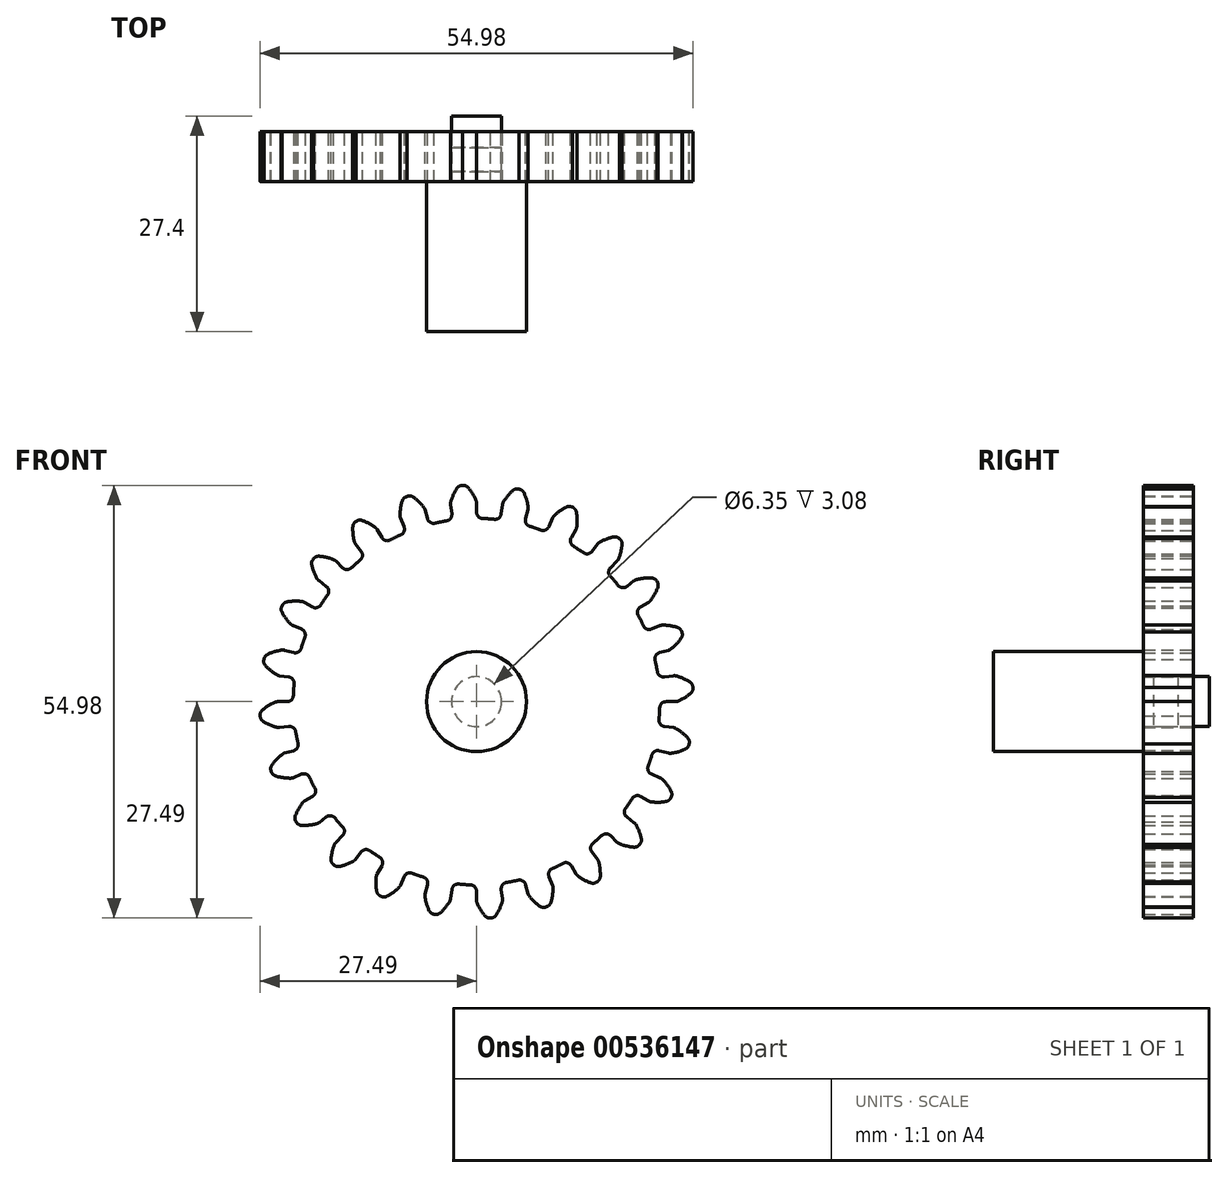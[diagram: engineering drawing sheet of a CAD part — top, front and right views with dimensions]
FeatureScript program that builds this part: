
annotation { "Feature Type Name" : "Feature", "Feature Type Description" : "" }
export const myFeature = defineFeature(function(context is Context, id is Id, definition is map)
    precondition{}
    {
        {
            var Q0;
            Q0=qCreatedBy(makeId("Front.planeOp"),FACE);
            var sketch = newSketch(context, id + "F0", { "sketchPlane" : qUnion([Q0])});
            skArc(sketch, "E0", {"start": v(-3.8, 22.97) * mm, "mid": v(-4.54, 22.84) * mm, "end": v(-5.28, 22.68) * mm});
            skArc(sketch, "E1.trimOffspring", {"start": v(-0.06, 25.55) * mm, "mid": v(-0.5, 26.41) * mm, "end": v(-1.06, 27.2) * mm});
            skLineSegment(sketch, "E2", {"start": v(0, 25.25) * mm, "end": v(0, 24.06) * mm});
            skLineSegment(sketch, "E3", {"start": v(-1.67, 27.49) * mm, "end": v(-1.8, 27.49) * mm});
            skLineSegment(sketch, "E4.MirrorCS", {"start": v(-1.93, 27.47) * mm, "end": v(-1.8, 27.49) * mm});
            skArc(sketch, "E5.MirrorCS", {"start": v(-3.28, 25.34) * mm, "mid": v(-2.95, 26.25) * mm, "end": v(-2.5, 27.1) * mm});
            skLineSegment(sketch, "E6.MirrorCS", {"start": v(-3.3, 25.03) * mm, "end": v(-3.14, 23.86) * mm});
            skPoint(sketch, "E7.visualSharp", {"position": v(-3.04, 23.08) * mm});
            skArc(sketch, "E8.filletArc", {"start": v(-3.8, 22.97) * mm, "mid": v(-3.3, 23.28) * mm, "end": v(-3.14, 23.86) * mm});
            skPoint(sketch, "E9.visualSharp", {"position": v(-3.32, 25.18) * mm});
            skArc(sketch, "E9.filletArc", {"start": v(-3.28, 25.34) * mm, "mid": v(-3.3, 25.19) * mm, "end": v(-3.3, 25.03) * mm});
            skPoint(sketch, "E10.visualSharp", {"position": v(-2.28, 27.42) * mm});
            skArc(sketch, "E10.filletArc", {"start": v(-1.93, 27.47) * mm, "mid": v(-2.25, 27.35) * mm, "end": v(-2.5, 27.1) * mm});
            skPoint(sketch, "E11.visualSharp", {"position": v(0, 25.4) * mm});
            skArc(sketch, "E11.filletArc", {"start": v(0, 25.25) * mm, "mid": v(-0.02, 25.4) * mm, "end": v(-0.06, 25.55) * mm});
            skPoint(sketch, "E12.visualSharp", {"position": v(0, 23.28) * mm});
            skArc(sketch, "E12.filletArc", {"start": v(0, 24.06) * mm, "mid": v(0.22, 23.51) * mm, "end": v(0.77, 23.27) * mm});
            skPoint(sketch, "E13.visualSharp", {"position": v(-1.31, 27.49) * mm});
            skArc(sketch, "E13.filletArc", {"start": v(-1.06, 27.2) * mm, "mid": v(-1.33, 27.41) * mm, "end": v(-1.67, 27.49) * mm});
            skArc(sketch, "E14.1.0", {"start": v(-9.61, 21.2) * mm, "mid": v(-9.2, 21.64) * mm, "end": v(-9.2, 22.23) * mm});
            skLineSegment(sketch, "E14.1.1", {"start": v(-9.66, 23.33) * mm, "end": v(-9.2, 22.23) * mm});
            skArc(sketch, "E14.1.2", {"start": v(-9.72, 23.63) * mm, "mid": v(-9.7, 23.47) * mm, "end": v(-9.66, 23.33) * mm});
            skArc(sketch, "E14.1.3", {"start": v(-9.72, 23.63) * mm, "mid": v(-9.65, 24.6) * mm, "end": v(-9.43, 25.54) * mm});
            skArc(sketch, "E14.1.4", {"start": v(-8.98, 26.03) * mm, "mid": v(-9.26, 25.83) * mm, "end": v(-9.43, 25.54) * mm});
            skLineSegment(sketch, "E14.1.5", {"start": v(-8.98, 26.03) * mm, "end": v(-8.85, 26.08) * mm});
            skLineSegment(sketch, "E14.1.6", {"start": v(-8.73, 26.12) * mm, "end": v(-8.85, 26.08) * mm});
            skArc(sketch, "E14.1.7", {"start": v(-8.07, 26) * mm, "mid": v(-8.38, 26.13) * mm, "end": v(-8.73, 26.12) * mm});
            skArc(sketch, "E14.1.8", {"start": v(-6.67, 24.67) * mm, "mid": v(-7.32, 25.39) * mm, "end": v(-8.07, 26) * mm});
            skArc(sketch, "E14.1.9", {"start": v(-6.53, 24.39) * mm, "mid": v(-6.59, 24.53) * mm, "end": v(-6.67, 24.67) * mm});
            skLineSegment(sketch, "E14.1.10", {"start": v(-6.53, 24.39) * mm, "end": v(-6.23, 23.24) * mm});
            skArc(sketch, "E14.1.11", {"start": v(-6.23, 23.24) * mm, "mid": v(-5.87, 22.77) * mm, "end": v(-5.28, 22.68) * mm});
            skArc(sketch, "E14.2.0", {"start": v(-14.78, 18) * mm, "mid": v(-14.5, 18.52) * mm, "end": v(-14.65, 19.1) * mm});
            skLineSegment(sketch, "E14.2.1", {"start": v(-15.37, 20.03) * mm, "end": v(-14.65, 19.1) * mm});
            skArc(sketch, "E14.2.2", {"start": v(-15.5, 20.3) * mm, "mid": v(-15.45, 20.16) * mm, "end": v(-15.37, 20.03) * mm});
            skArc(sketch, "E14.2.3", {"start": v(-15.5, 20.3) * mm, "mid": v(-15.69, 21.26) * mm, "end": v(-15.72, 22.23) * mm});
            skArc(sketch, "E14.2.4", {"start": v(-15.4, 22.82) * mm, "mid": v(-15.63, 22.56) * mm, "end": v(-15.72, 22.23) * mm});
            skLineSegment(sketch, "E14.2.5", {"start": v(-15.4, 22.82) * mm, "end": v(-15.3, 22.9) * mm});
            skLineSegment(sketch, "E14.2.6", {"start": v(-15.19, 22.97) * mm, "end": v(-15.3, 22.9) * mm});
            skArc(sketch, "E14.2.7", {"start": v(-14.52, 23.03) * mm, "mid": v(-14.86, 23.07) * mm, "end": v(-15.19, 22.97) * mm});
            skArc(sketch, "E14.2.8", {"start": v(-12.83, 22.1) * mm, "mid": v(-13.64, 22.63) * mm, "end": v(-14.52, 23.03) * mm});
            skArc(sketch, "E14.2.9", {"start": v(-12.62, 21.87) * mm, "mid": v(-12.71, 22) * mm, "end": v(-12.83, 22.1) * mm});
            skLineSegment(sketch, "E14.2.10", {"start": v(-12.62, 21.87) * mm, "end": v(-12.03, 20.84) * mm});
            skArc(sketch, "E14.2.11", {"start": v(-12.03, 20.84) * mm, "mid": v(-11.56, 20.47) * mm, "end": v(-10.97, 20.54) * mm});
            skArc(sketch, "E15.2.3.0", {"start": v(-18.93, 13.56) * mm, "mid": v(-18.79, 14.14) * mm, "end": v(-19.1, 14.65) * mm});
            skLineSegment(sketch, "E15.4.3.0", {"start": v(-20.03, 15.37) * mm, "end": v(-19.1, 14.65) * mm});
            skArc(sketch, "E15.7.3.0", {"start": v(-20.23, 15.6) * mm, "mid": v(-20.14, 15.48) * mm, "end": v(-20.03, 15.37) * mm});
            skArc(sketch, "E15.11.3.0", {"start": v(-20.23, 15.6) * mm, "mid": v(-20.65, 16.48) * mm, "end": v(-20.93, 17.4) * mm});
            skArc(sketch, "E15.15.3.0", {"start": v(-20.79, 18.06) * mm, "mid": v(-20.93, 17.75) * mm, "end": v(-20.93, 17.4) * mm});
            skLineSegment(sketch, "E15.19.3.0", {"start": v(-20.79, 18.06) * mm, "end": v(-20.7, 18.16) * mm});
            skLineSegment(sketch, "E15.22.3.0", {"start": v(-20.62, 18.25) * mm, "end": v(-20.7, 18.16) * mm});
            skArc(sketch, "E15.25.3.0", {"start": v(-19.99, 18.48) * mm, "mid": v(-20.33, 18.44) * mm, "end": v(-20.62, 18.25) * mm});
            skArc(sketch, "E15.29.3.0", {"start": v(-18.11, 18.02) * mm, "mid": v(-19.03, 18.33) * mm, "end": v(-19.99, 18.48) * mm});
            skArc(sketch, "E15.33.3.0", {"start": v(-17.85, 17.85) * mm, "mid": v(-17.97, 17.95) * mm, "end": v(-18.11, 18.02) * mm});
            skLineSegment(sketch, "E15.37.3.0", {"start": v(-17.85, 17.85) * mm, "end": v(-17.02, 17.02) * mm});
            skArc(sketch, "E15.40.3.0", {"start": v(-17.02, 17.02) * mm, "mid": v(-16.47, 16.78) * mm, "end": v(-15.91, 17) * mm});
            skArc(sketch, "E15.2.4.0", {"start": v(-21.8, 8.2) * mm, "mid": v(-21.8, 8.8) * mm, "end": v(-22.23, 9.2) * mm});
            skLineSegment(sketch, "E15.4.4.0", {"start": v(-23.33, 9.66) * mm, "end": v(-22.23, 9.2) * mm});
            skArc(sketch, "E15.7.4.0", {"start": v(-23.58, 9.83) * mm, "mid": v(-23.46, 9.74) * mm, "end": v(-23.33, 9.66) * mm});
            skArc(sketch, "E15.11.4.0", {"start": v(-23.58, 9.83) * mm, "mid": v(-24.21, 10.57) * mm, "end": v(-24.72, 11.4) * mm});
            skArc(sketch, "E15.15.4.0", {"start": v(-24.75, 12.06) * mm, "mid": v(-24.81, 11.72) * mm, "end": v(-24.72, 11.4) * mm});
            skLineSegment(sketch, "E15.19.4.0", {"start": v(-24.75, 12.06) * mm, "end": v(-24.7, 12.18) * mm});
            skLineSegment(sketch, "E15.22.4.0", {"start": v(-24.64, 12.3) * mm, "end": v(-24.7, 12.18) * mm});
            skArc(sketch, "E15.25.4.0", {"start": v(-24.09, 12.68) * mm, "mid": v(-24.4, 12.55) * mm, "end": v(-24.64, 12.3) * mm});
            skArc(sketch, "E15.29.4.0", {"start": v(-22.16, 12.72) * mm, "mid": v(-23.12, 12.78) * mm, "end": v(-24.09, 12.68) * mm});
            skArc(sketch, "E15.33.4.0", {"start": v(-21.87, 12.62) * mm, "mid": v(-22, 12.69) * mm, "end": v(-22.16, 12.72) * mm});
            skLineSegment(sketch, "E15.37.4.0", {"start": v(-21.87, 12.62) * mm, "end": v(-20.84, 12.03) * mm});
            skArc(sketch, "E15.40.4.0", {"start": v(-20.84, 12.03) * mm, "mid": v(-20.25, 11.95) * mm, "end": v(-19.77, 12.3) * mm});
            skArc(sketch, "E15.2.5.0", {"start": v(-23.17, 2.28) * mm, "mid": v(-23.34, 2.85) * mm, "end": v(-23.86, 3.14) * mm});
            skLineSegment(sketch, "E15.4.5.0", {"start": v(-25.03, 3.3) * mm, "end": v(-23.86, 3.14) * mm});
            skArc(sketch, "E15.7.5.0", {"start": v(-25.32, 3.4) * mm, "mid": v(-25.18, 3.33) * mm, "end": v(-25.03, 3.3) * mm});
            skArc(sketch, "E15.11.5.0", {"start": v(-25.32, 3.4) * mm, "mid": v(-26.12, 3.94) * mm, "end": v(-26.83, 4.6) * mm});
            skArc(sketch, "E15.15.5.0", {"start": v(-27.03, 5.24) * mm, "mid": v(-27, 4.9) * mm, "end": v(-26.83, 4.6) * mm});
            skLineSegment(sketch, "E15.19.5.0", {"start": v(-27.03, 5.24) * mm, "end": v(-27.01, 5.37) * mm});
            skLineSegment(sketch, "E15.22.5.0", {"start": v(-26.98, 5.5) * mm, "end": v(-27.01, 5.37) * mm});
            skArc(sketch, "E15.25.5.0", {"start": v(-26.55, 6.01) * mm, "mid": v(-26.82, 5.8) * mm, "end": v(-26.98, 5.5) * mm});
            skArc(sketch, "E15.29.5.0", {"start": v(-24.7, 6.55) * mm, "mid": v(-25.64, 6.36) * mm, "end": v(-26.55, 6.01) * mm});
            skArc(sketch, "E15.33.5.0", {"start": v(-24.39, 6.53) * mm, "mid": v(-24.54, 6.56) * mm, "end": v(-24.7, 6.55) * mm});
            skLineSegment(sketch, "E15.37.5.0", {"start": v(-24.39, 6.53) * mm, "end": v(-23.24, 6.23) * mm});
            skArc(sketch, "E15.40.5.0", {"start": v(-23.24, 6.23) * mm, "mid": v(-22.65, 6.3) * mm, "end": v(-22.28, 6.76) * mm});
            skArc(sketch, "E15.2.6.0", {"start": v(-22.97, -3.8) * mm, "mid": v(-23.28, -3.3) * mm, "end": v(-23.86, -3.14) * mm});
            skLineSegment(sketch, "E15.4.6.0", {"start": v(-25.03, -3.3) * mm, "end": v(-23.86, -3.14) * mm});
            skArc(sketch, "E15.7.6.0", {"start": v(-25.34, -3.28) * mm, "mid": v(-25.19, -3.3) * mm, "end": v(-25.03, -3.3) * mm});
            skArc(sketch, "E15.11.6.0", {"start": v(-25.34, -3.28) * mm, "mid": v(-26.25, -2.95) * mm, "end": v(-27.1, -2.5) * mm});
            skArc(sketch, "E15.15.6.0", {"start": v(-27.47, -1.93) * mm, "mid": v(-27.35, -2.25) * mm, "end": v(-27.1, -2.5) * mm});
            skLineSegment(sketch, "E15.19.6.0", {"start": v(-27.47, -1.93) * mm, "end": v(-27.49, -1.8) * mm});
            skLineSegment(sketch, "E15.22.6.0", {"start": v(-27.49, -1.67) * mm, "end": v(-27.49, -1.8) * mm});
            skArc(sketch, "E15.25.6.0", {"start": v(-27.2, -1.06) * mm, "mid": v(-27.41, -1.33) * mm, "end": v(-27.49, -1.67) * mm});
            skArc(sketch, "E15.29.6.0", {"start": v(-25.55, -0.06) * mm, "mid": v(-26.41, -0.5) * mm, "end": v(-27.2, -1.06) * mm});
            skArc(sketch, "E15.33.6.0", {"start": v(-25.25, 0) * mm, "mid": v(-25.4, -0.02) * mm, "end": v(-25.55, -0.06) * mm});
            skLineSegment(sketch, "E15.37.6.0", {"start": v(-25.25, 0) * mm, "end": v(-24.06, 0) * mm});
            skArc(sketch, "E15.40.6.0", {"start": v(-24.06, 0) * mm, "mid": v(-23.51, 0.22) * mm, "end": v(-23.27, 0.77) * mm});
            skArc(sketch, "E15.2.7.0", {"start": v(-21.2, -9.61) * mm, "mid": v(-21.64, -9.2) * mm, "end": v(-22.23, -9.2) * mm});
            skLineSegment(sketch, "E15.4.7.0", {"start": v(-23.33, -9.66) * mm, "end": v(-22.23, -9.2) * mm});
            skArc(sketch, "E15.7.7.0", {"start": v(-23.63, -9.72) * mm, "mid": v(-23.47, -9.7) * mm, "end": v(-23.33, -9.66) * mm});
            skArc(sketch, "E15.11.7.0", {"start": v(-23.63, -9.72) * mm, "mid": v(-24.6, -9.65) * mm, "end": v(-25.54, -9.43) * mm});
            skArc(sketch, "E15.15.7.0", {"start": v(-26.03, -8.98) * mm, "mid": v(-25.83, -9.26) * mm, "end": v(-25.54, -9.43) * mm});
            skLineSegment(sketch, "E15.19.7.0", {"start": v(-26.03, -8.98) * mm, "end": v(-26.08, -8.85) * mm});
            skLineSegment(sketch, "E15.22.7.0", {"start": v(-26.12, -8.73) * mm, "end": v(-26.08, -8.85) * mm});
            skArc(sketch, "E15.25.7.0", {"start": v(-26, -8.07) * mm, "mid": v(-26.13, -8.38) * mm, "end": v(-26.12, -8.73) * mm});
            skArc(sketch, "E15.29.7.0", {"start": v(-24.67, -6.67) * mm, "mid": v(-25.39, -7.32) * mm, "end": v(-26, -8.07) * mm});
            skArc(sketch, "E15.33.7.0", {"start": v(-24.39, -6.53) * mm, "mid": v(-24.53, -6.59) * mm, "end": v(-24.67, -6.67) * mm});
            skLineSegment(sketch, "E15.37.7.0", {"start": v(-24.39, -6.53) * mm, "end": v(-23.24, -6.23) * mm});
            skArc(sketch, "E15.40.7.0", {"start": v(-23.24, -6.23) * mm, "mid": v(-22.77, -5.87) * mm, "end": v(-22.68, -5.28) * mm});
            skArc(sketch, "E15.2.8.0", {"start": v(-18, -14.78) * mm, "mid": v(-18.52, -14.5) * mm, "end": v(-19.1, -14.65) * mm});
            skLineSegment(sketch, "E15.4.8.0", {"start": v(-20.03, -15.37) * mm, "end": v(-19.1, -14.65) * mm});
            skArc(sketch, "E15.7.8.0", {"start": v(-20.3, -15.5) * mm, "mid": v(-20.16, -15.45) * mm, "end": v(-20.03, -15.37) * mm});
            skArc(sketch, "E15.11.8.0", {"start": v(-20.3, -15.5) * mm, "mid": v(-21.26, -15.69) * mm, "end": v(-22.23, -15.72) * mm});
            skArc(sketch, "E15.15.8.0", {"start": v(-22.82, -15.4) * mm, "mid": v(-22.56, -15.63) * mm, "end": v(-22.23, -15.72) * mm});
            skLineSegment(sketch, "E15.19.8.0", {"start": v(-22.82, -15.4) * mm, "end": v(-22.9, -15.3) * mm});
            skLineSegment(sketch, "E15.22.8.0", {"start": v(-22.97, -15.19) * mm, "end": v(-22.9, -15.3) * mm});
            skArc(sketch, "E15.25.8.0", {"start": v(-23.03, -14.52) * mm, "mid": v(-23.07, -14.86) * mm, "end": v(-22.97, -15.19) * mm});
            skArc(sketch, "E15.29.8.0", {"start": v(-22.1, -12.83) * mm, "mid": v(-22.63, -13.64) * mm, "end": v(-23.03, -14.52) * mm});
            skArc(sketch, "E15.33.8.0", {"start": v(-21.87, -12.62) * mm, "mid": v(-22, -12.71) * mm, "end": v(-22.1, -12.83) * mm});
            skLineSegment(sketch, "E15.37.8.0", {"start": v(-21.87, -12.62) * mm, "end": v(-20.84, -12.03) * mm});
            skArc(sketch, "E15.40.8.0", {"start": v(-20.84, -12.03) * mm, "mid": v(-20.47, -11.56) * mm, "end": v(-20.54, -10.97) * mm});
            skArc(sketch, "E15.2.9.0", {"start": v(-13.56, -18.93) * mm, "mid": v(-14.14, -18.79) * mm, "end": v(-14.65, -19.1) * mm});
            skLineSegment(sketch, "E15.4.9.0", {"start": v(-15.37, -20.03) * mm, "end": v(-14.65, -19.1) * mm});
            skArc(sketch, "E15.7.9.0", {"start": v(-15.6, -20.23) * mm, "mid": v(-15.48, -20.14) * mm, "end": v(-15.37, -20.03) * mm});
            skArc(sketch, "E15.11.9.0", {"start": v(-15.6, -20.23) * mm, "mid": v(-16.48, -20.65) * mm, "end": v(-17.4, -20.93) * mm});
            skArc(sketch, "E15.15.9.0", {"start": v(-18.06, -20.79) * mm, "mid": v(-17.75, -20.93) * mm, "end": v(-17.4, -20.93) * mm});
            skLineSegment(sketch, "E15.19.9.0", {"start": v(-18.06, -20.79) * mm, "end": v(-18.16, -20.7) * mm});
            skLineSegment(sketch, "E15.22.9.0", {"start": v(-18.25, -20.62) * mm, "end": v(-18.16, -20.7) * mm});
            skArc(sketch, "E15.25.9.0", {"start": v(-18.48, -19.99) * mm, "mid": v(-18.44, -20.33) * mm, "end": v(-18.25, -20.62) * mm});
            skArc(sketch, "E15.29.9.0", {"start": v(-18.02, -18.11) * mm, "mid": v(-18.33, -19.03) * mm, "end": v(-18.48, -19.99) * mm});
            skArc(sketch, "E15.33.9.0", {"start": v(-17.85, -17.85) * mm, "mid": v(-17.95, -17.97) * mm, "end": v(-18.02, -18.11) * mm});
            skLineSegment(sketch, "E15.37.9.0", {"start": v(-17.85, -17.85) * mm, "end": v(-17.02, -17.02) * mm});
            skArc(sketch, "E15.40.9.0", {"start": v(-17.02, -17.02) * mm, "mid": v(-16.78, -16.47) * mm, "end": v(-17, -15.91) * mm});
            skArc(sketch, "E15.2.10.0", {"start": v(-8.2, -21.8) * mm, "mid": v(-8.8, -21.8) * mm, "end": v(-9.2, -22.23) * mm});
            skLineSegment(sketch, "E15.4.10.0", {"start": v(-9.66, -23.33) * mm, "end": v(-9.2, -22.23) * mm});
            skArc(sketch, "E15.7.10.0", {"start": v(-9.83, -23.58) * mm, "mid": v(-9.74, -23.46) * mm, "end": v(-9.66, -23.33) * mm});
            skArc(sketch, "E15.11.10.0", {"start": v(-9.83, -23.58) * mm, "mid": v(-10.57, -24.21) * mm, "end": v(-11.4, -24.72) * mm});
            skArc(sketch, "E15.15.10.0", {"start": v(-12.06, -24.75) * mm, "mid": v(-11.72, -24.81) * mm, "end": v(-11.4, -24.72) * mm});
            skLineSegment(sketch, "E15.19.10.0", {"start": v(-12.06, -24.75) * mm, "end": v(-12.18, -24.7) * mm});
            skLineSegment(sketch, "E15.22.10.0", {"start": v(-12.3, -24.64) * mm, "end": v(-12.18, -24.7) * mm});
            skArc(sketch, "E15.25.10.0", {"start": v(-12.68, -24.09) * mm, "mid": v(-12.55, -24.4) * mm, "end": v(-12.3, -24.64) * mm});
            skArc(sketch, "E15.29.10.0", {"start": v(-12.72, -22.16) * mm, "mid": v(-12.78, -23.12) * mm, "end": v(-12.68, -24.09) * mm});
            skArc(sketch, "E15.33.10.0", {"start": v(-12.62, -21.87) * mm, "mid": v(-12.69, -22) * mm, "end": v(-12.72, -22.16) * mm});
            skLineSegment(sketch, "E15.37.10.0", {"start": v(-12.62, -21.87) * mm, "end": v(-12.03, -20.84) * mm});
            skArc(sketch, "E15.40.10.0", {"start": v(-12.03, -20.84) * mm, "mid": v(-11.95, -20.25) * mm, "end": v(-12.3, -19.77) * mm});
            skArc(sketch, "E15.2.11.0", {"start": v(-2.28, -23.17) * mm, "mid": v(-2.85, -23.34) * mm, "end": v(-3.14, -23.86) * mm});
            skLineSegment(sketch, "E15.4.11.0", {"start": v(-3.3, -25.03) * mm, "end": v(-3.14, -23.86) * mm});
            skArc(sketch, "E15.7.11.0", {"start": v(-3.4, -25.32) * mm, "mid": v(-3.33, -25.18) * mm, "end": v(-3.3, -25.03) * mm});
            skArc(sketch, "E15.11.11.0", {"start": v(-3.4, -25.32) * mm, "mid": v(-3.94, -26.12) * mm, "end": v(-4.6, -26.83) * mm});
            skArc(sketch, "E15.15.11.0", {"start": v(-5.24, -27.03) * mm, "mid": v(-4.9, -27) * mm, "end": v(-4.6, -26.83) * mm});
            skLineSegment(sketch, "E15.19.11.0", {"start": v(-5.24, -27.03) * mm, "end": v(-5.37, -27.01) * mm});
            skLineSegment(sketch, "E15.22.11.0", {"start": v(-5.5, -26.98) * mm, "end": v(-5.37, -27.01) * mm});
            skArc(sketch, "E15.25.11.0", {"start": v(-6.01, -26.55) * mm, "mid": v(-5.8, -26.82) * mm, "end": v(-5.5, -26.98) * mm});
            skArc(sketch, "E15.29.11.0", {"start": v(-6.55, -24.7) * mm, "mid": v(-6.36, -25.64) * mm, "end": v(-6.01, -26.55) * mm});
            skArc(sketch, "E15.33.11.0", {"start": v(-6.53, -24.39) * mm, "mid": v(-6.56, -24.54) * mm, "end": v(-6.55, -24.7) * mm});
            skLineSegment(sketch, "E15.37.11.0", {"start": v(-6.53, -24.39) * mm, "end": v(-6.23, -23.24) * mm});
            skArc(sketch, "E15.40.11.0", {"start": v(-6.23, -23.24) * mm, "mid": v(-6.3, -22.65) * mm, "end": v(-6.76, -22.28) * mm});
            skArc(sketch, "E15.2.12.0", {"start": v(3.8, -22.97) * mm, "mid": v(3.3, -23.28) * mm, "end": v(3.14, -23.86) * mm});
            skLineSegment(sketch, "E15.4.12.0", {"start": v(3.3, -25.03) * mm, "end": v(3.14, -23.86) * mm});
            skArc(sketch, "E15.7.12.0", {"start": v(3.28, -25.34) * mm, "mid": v(3.3, -25.19) * mm, "end": v(3.3, -25.03) * mm});
            skArc(sketch, "E15.11.12.0", {"start": v(3.28, -25.34) * mm, "mid": v(2.95, -26.25) * mm, "end": v(2.5, -27.1) * mm});
            skArc(sketch, "E15.15.12.0", {"start": v(1.93, -27.47) * mm, "mid": v(2.25, -27.35) * mm, "end": v(2.5, -27.1) * mm});
            skLineSegment(sketch, "E15.19.12.0", {"start": v(1.93, -27.47) * mm, "end": v(1.8, -27.49) * mm});
            skLineSegment(sketch, "E15.22.12.0", {"start": v(1.67, -27.49) * mm, "end": v(1.8, -27.49) * mm});
            skArc(sketch, "E15.25.12.0", {"start": v(1.06, -27.2) * mm, "mid": v(1.33, -27.41) * mm, "end": v(1.67, -27.49) * mm});
            skArc(sketch, "E15.29.12.0", {"start": v(0.06, -25.55) * mm, "mid": v(0.5, -26.41) * mm, "end": v(1.06, -27.2) * mm});
            skArc(sketch, "E15.33.12.0", {"start": v(0, -25.25) * mm, "mid": v(0.02, -25.4) * mm, "end": v(0.06, -25.55) * mm});
            skLineSegment(sketch, "E15.37.12.0", {"start": v(0, -25.25) * mm, "end": v(0, -24.06) * mm});
            skArc(sketch, "E15.40.12.0", {"start": v(0, -24.06) * mm, "mid": v(-0.22, -23.51) * mm, "end": v(-0.77, -23.27) * mm});
            skArc(sketch, "E15.2.13.0", {"start": v(9.61, -21.2) * mm, "mid": v(9.2, -21.64) * mm, "end": v(9.2, -22.23) * mm});
            skLineSegment(sketch, "E15.4.13.0", {"start": v(9.66, -23.33) * mm, "end": v(9.2, -22.23) * mm});
            skArc(sketch, "E15.7.13.0", {"start": v(9.72, -23.63) * mm, "mid": v(9.7, -23.47) * mm, "end": v(9.66, -23.33) * mm});
            skArc(sketch, "E15.11.13.0", {"start": v(9.72, -23.63) * mm, "mid": v(9.65, -24.6) * mm, "end": v(9.43, -25.54) * mm});
            skArc(sketch, "E15.15.13.0", {"start": v(8.98, -26.03) * mm, "mid": v(9.26, -25.83) * mm, "end": v(9.43, -25.54) * mm});
            skLineSegment(sketch, "E15.19.13.0", {"start": v(8.98, -26.03) * mm, "end": v(8.85, -26.08) * mm});
            skLineSegment(sketch, "E15.22.13.0", {"start": v(8.73, -26.12) * mm, "end": v(8.85, -26.08) * mm});
            skArc(sketch, "E15.25.13.0", {"start": v(8.07, -26) * mm, "mid": v(8.38, -26.13) * mm, "end": v(8.73, -26.12) * mm});
            skArc(sketch, "E15.29.13.0", {"start": v(6.67, -24.67) * mm, "mid": v(7.32, -25.39) * mm, "end": v(8.07, -26) * mm});
            skArc(sketch, "E15.33.13.0", {"start": v(6.53, -24.39) * mm, "mid": v(6.59, -24.53) * mm, "end": v(6.67, -24.67) * mm});
            skLineSegment(sketch, "E15.37.13.0", {"start": v(6.53, -24.39) * mm, "end": v(6.23, -23.24) * mm});
            skArc(sketch, "E15.40.13.0", {"start": v(6.23, -23.24) * mm, "mid": v(5.87, -22.77) * mm, "end": v(5.28, -22.68) * mm});
            skArc(sketch, "E15.2.14.0", {"start": v(14.78, -18) * mm, "mid": v(14.5, -18.52) * mm, "end": v(14.65, -19.1) * mm});
            skLineSegment(sketch, "E15.4.14.0", {"start": v(15.37, -20.03) * mm, "end": v(14.65, -19.1) * mm});
            skArc(sketch, "E15.7.14.0", {"start": v(15.5, -20.3) * mm, "mid": v(15.45, -20.16) * mm, "end": v(15.37, -20.03) * mm});
            skArc(sketch, "E15.11.14.0", {"start": v(15.5, -20.3) * mm, "mid": v(15.69, -21.26) * mm, "end": v(15.72, -22.23) * mm});
            skArc(sketch, "E15.15.14.0", {"start": v(15.4, -22.82) * mm, "mid": v(15.63, -22.56) * mm, "end": v(15.72, -22.23) * mm});
            skLineSegment(sketch, "E15.19.14.0", {"start": v(15.4, -22.82) * mm, "end": v(15.3, -22.9) * mm});
            skLineSegment(sketch, "E15.22.14.0", {"start": v(15.19, -22.97) * mm, "end": v(15.3, -22.9) * mm});
            skArc(sketch, "E15.25.14.0", {"start": v(14.52, -23.03) * mm, "mid": v(14.86, -23.07) * mm, "end": v(15.19, -22.97) * mm});
            skArc(sketch, "E15.29.14.0", {"start": v(12.83, -22.1) * mm, "mid": v(13.64, -22.63) * mm, "end": v(14.52, -23.03) * mm});
            skArc(sketch, "E15.33.14.0", {"start": v(12.62, -21.87) * mm, "mid": v(12.71, -22) * mm, "end": v(12.83, -22.1) * mm});
            skLineSegment(sketch, "E15.37.14.0", {"start": v(12.62, -21.87) * mm, "end": v(12.03, -20.84) * mm});
            skArc(sketch, "E15.40.14.0", {"start": v(12.03, -20.84) * mm, "mid": v(11.56, -20.47) * mm, "end": v(10.97, -20.54) * mm});
            skArc(sketch, "E15.2.15.0", {"start": v(18.93, -13.56) * mm, "mid": v(18.79, -14.14) * mm, "end": v(19.1, -14.65) * mm});
            skLineSegment(sketch, "E15.4.15.0", {"start": v(20.03, -15.37) * mm, "end": v(19.1, -14.65) * mm});
            skArc(sketch, "E15.7.15.0", {"start": v(20.23, -15.6) * mm, "mid": v(20.14, -15.48) * mm, "end": v(20.03, -15.37) * mm});
            skArc(sketch, "E15.11.15.0", {"start": v(20.23, -15.6) * mm, "mid": v(20.65, -16.48) * mm, "end": v(20.93, -17.4) * mm});
            skArc(sketch, "E15.15.15.0", {"start": v(20.79, -18.06) * mm, "mid": v(20.93, -17.75) * mm, "end": v(20.93, -17.4) * mm});
            skLineSegment(sketch, "E15.19.15.0", {"start": v(20.79, -18.06) * mm, "end": v(20.7, -18.16) * mm});
            skLineSegment(sketch, "E15.22.15.0", {"start": v(20.62, -18.25) * mm, "end": v(20.7, -18.16) * mm});
            skArc(sketch, "E15.25.15.0", {"start": v(19.99, -18.48) * mm, "mid": v(20.33, -18.44) * mm, "end": v(20.62, -18.25) * mm});
            skArc(sketch, "E15.29.15.0", {"start": v(18.11, -18.02) * mm, "mid": v(19.03, -18.33) * mm, "end": v(19.99, -18.48) * mm});
            skArc(sketch, "E15.33.15.0", {"start": v(17.85, -17.85) * mm, "mid": v(17.97, -17.95) * mm, "end": v(18.11, -18.02) * mm});
            skLineSegment(sketch, "E15.37.15.0", {"start": v(17.85, -17.85) * mm, "end": v(17.02, -17.02) * mm});
            skArc(sketch, "E15.40.15.0", {"start": v(17.02, -17.02) * mm, "mid": v(16.47, -16.78) * mm, "end": v(15.91, -17) * mm});
            skArc(sketch, "E15.2.16.0", {"start": v(21.8, -8.2) * mm, "mid": v(21.8, -8.8) * mm, "end": v(22.23, -9.2) * mm});
            skLineSegment(sketch, "E15.4.16.0", {"start": v(23.33, -9.66) * mm, "end": v(22.23, -9.2) * mm});
            skArc(sketch, "E15.7.16.0", {"start": v(23.58, -9.83) * mm, "mid": v(23.46, -9.74) * mm, "end": v(23.33, -9.66) * mm});
            skArc(sketch, "E15.11.16.0", {"start": v(23.58, -9.83) * mm, "mid": v(24.21, -10.57) * mm, "end": v(24.72, -11.4) * mm});
            skArc(sketch, "E15.15.16.0", {"start": v(24.75, -12.06) * mm, "mid": v(24.81, -11.72) * mm, "end": v(24.72, -11.4) * mm});
            skLineSegment(sketch, "E15.19.16.0", {"start": v(24.75, -12.06) * mm, "end": v(24.7, -12.18) * mm});
            skLineSegment(sketch, "E15.22.16.0", {"start": v(24.64, -12.3) * mm, "end": v(24.7, -12.18) * mm});
            skArc(sketch, "E15.25.16.0", {"start": v(24.09, -12.68) * mm, "mid": v(24.4, -12.55) * mm, "end": v(24.64, -12.3) * mm});
            skArc(sketch, "E15.29.16.0", {"start": v(22.16, -12.72) * mm, "mid": v(23.12, -12.78) * mm, "end": v(24.09, -12.68) * mm});
            skArc(sketch, "E15.33.16.0", {"start": v(21.87, -12.62) * mm, "mid": v(22, -12.69) * mm, "end": v(22.16, -12.72) * mm});
            skLineSegment(sketch, "E15.37.16.0", {"start": v(21.87, -12.62) * mm, "end": v(20.84, -12.03) * mm});
            skArc(sketch, "E15.40.16.0", {"start": v(20.84, -12.03) * mm, "mid": v(20.25, -11.95) * mm, "end": v(19.77, -12.3) * mm});
            skArc(sketch, "E15.2.17.0", {"start": v(23.17, -2.28) * mm, "mid": v(23.34, -2.85) * mm, "end": v(23.86, -3.14) * mm});
            skLineSegment(sketch, "E15.4.17.0", {"start": v(25.03, -3.3) * mm, "end": v(23.86, -3.14) * mm});
            skArc(sketch, "E15.7.17.0", {"start": v(25.32, -3.4) * mm, "mid": v(25.18, -3.33) * mm, "end": v(25.03, -3.3) * mm});
            skArc(sketch, "E15.11.17.0", {"start": v(25.32, -3.4) * mm, "mid": v(26.12, -3.94) * mm, "end": v(26.83, -4.6) * mm});
            skArc(sketch, "E15.15.17.0", {"start": v(27.03, -5.24) * mm, "mid": v(27, -4.9) * mm, "end": v(26.83, -4.6) * mm});
            skLineSegment(sketch, "E15.19.17.0", {"start": v(27.03, -5.24) * mm, "end": v(27.01, -5.37) * mm});
            skLineSegment(sketch, "E15.22.17.0", {"start": v(26.98, -5.5) * mm, "end": v(27.01, -5.37) * mm});
            skArc(sketch, "E15.25.17.0", {"start": v(26.55, -6.01) * mm, "mid": v(26.82, -5.8) * mm, "end": v(26.98, -5.5) * mm});
            skArc(sketch, "E15.29.17.0", {"start": v(24.7, -6.55) * mm, "mid": v(25.64, -6.36) * mm, "end": v(26.55, -6.01) * mm});
            skArc(sketch, "E15.33.17.0", {"start": v(24.39, -6.53) * mm, "mid": v(24.54, -6.56) * mm, "end": v(24.7, -6.55) * mm});
            skLineSegment(sketch, "E15.37.17.0", {"start": v(24.39, -6.53) * mm, "end": v(23.24, -6.23) * mm});
            skArc(sketch, "E15.40.17.0", {"start": v(23.24, -6.23) * mm, "mid": v(22.65, -6.3) * mm, "end": v(22.28, -6.76) * mm});
            skArc(sketch, "E15.2.18.0", {"start": v(22.97, 3.8) * mm, "mid": v(23.28, 3.3) * mm, "end": v(23.86, 3.14) * mm});
            skLineSegment(sketch, "E15.4.18.0", {"start": v(25.03, 3.3) * mm, "end": v(23.86, 3.14) * mm});
            skArc(sketch, "E15.7.18.0", {"start": v(25.34, 3.28) * mm, "mid": v(25.19, 3.3) * mm, "end": v(25.03, 3.3) * mm});
            skArc(sketch, "E15.11.18.0", {"start": v(25.34, 3.28) * mm, "mid": v(26.25, 2.95) * mm, "end": v(27.1, 2.5) * mm});
            skArc(sketch, "E15.15.18.0", {"start": v(27.47, 1.93) * mm, "mid": v(27.35, 2.25) * mm, "end": v(27.1, 2.5) * mm});
            skLineSegment(sketch, "E15.19.18.0", {"start": v(27.47, 1.93) * mm, "end": v(27.49, 1.8) * mm});
            skLineSegment(sketch, "E15.22.18.0", {"start": v(27.49, 1.67) * mm, "end": v(27.49, 1.8) * mm});
            skArc(sketch, "E15.25.18.0", {"start": v(27.2, 1.06) * mm, "mid": v(27.41, 1.33) * mm, "end": v(27.49, 1.67) * mm});
            skArc(sketch, "E15.29.18.0", {"start": v(25.55, 0.06) * mm, "mid": v(26.41, 0.5) * mm, "end": v(27.2, 1.06) * mm});
            skArc(sketch, "E15.33.18.0", {"start": v(25.25, 0) * mm, "mid": v(25.4, 0.02) * mm, "end": v(25.55, 0.06) * mm});
            skLineSegment(sketch, "E15.37.18.0", {"start": v(25.25, 0) * mm, "end": v(24.06, 0) * mm});
            skArc(sketch, "E15.40.18.0", {"start": v(24.06, 0) * mm, "mid": v(23.51, -0.22) * mm, "end": v(23.27, -0.77) * mm});
            skArc(sketch, "E15.2.19.0", {"start": v(21.2, 9.61) * mm, "mid": v(21.64, 9.2) * mm, "end": v(22.23, 9.2) * mm});
            skLineSegment(sketch, "E15.4.19.0", {"start": v(23.33, 9.66) * mm, "end": v(22.23, 9.2) * mm});
            skArc(sketch, "E15.7.19.0", {"start": v(23.63, 9.72) * mm, "mid": v(23.47, 9.7) * mm, "end": v(23.33, 9.66) * mm});
            skArc(sketch, "E15.11.19.0", {"start": v(23.63, 9.72) * mm, "mid": v(24.6, 9.65) * mm, "end": v(25.54, 9.43) * mm});
            skArc(sketch, "E15.15.19.0", {"start": v(26.03, 8.98) * mm, "mid": v(25.83, 9.26) * mm, "end": v(25.54, 9.43) * mm});
            skLineSegment(sketch, "E15.19.19.0", {"start": v(26.03, 8.98) * mm, "end": v(26.08, 8.85) * mm});
            skLineSegment(sketch, "E15.22.19.0", {"start": v(26.12, 8.73) * mm, "end": v(26.08, 8.85) * mm});
            skArc(sketch, "E15.25.19.0", {"start": v(26, 8.07) * mm, "mid": v(26.13, 8.38) * mm, "end": v(26.12, 8.73) * mm});
            skArc(sketch, "E15.29.19.0", {"start": v(24.67, 6.67) * mm, "mid": v(25.39, 7.32) * mm, "end": v(26, 8.07) * mm});
            skArc(sketch, "E15.33.19.0", {"start": v(24.39, 6.53) * mm, "mid": v(24.53, 6.59) * mm, "end": v(24.67, 6.67) * mm});
            skLineSegment(sketch, "E15.37.19.0", {"start": v(24.39, 6.53) * mm, "end": v(23.24, 6.23) * mm});
            skArc(sketch, "E15.40.19.0", {"start": v(23.24, 6.23) * mm, "mid": v(22.77, 5.87) * mm, "end": v(22.68, 5.28) * mm});
            skArc(sketch, "E15.2.20.0", {"start": v(18, 14.78) * mm, "mid": v(18.52, 14.5) * mm, "end": v(19.1, 14.65) * mm});
            skLineSegment(sketch, "E15.4.20.0", {"start": v(20.03, 15.37) * mm, "end": v(19.1, 14.65) * mm});
            skArc(sketch, "E15.7.20.0", {"start": v(20.3, 15.5) * mm, "mid": v(20.16, 15.45) * mm, "end": v(20.03, 15.37) * mm});
            skArc(sketch, "E15.11.20.0", {"start": v(20.3, 15.5) * mm, "mid": v(21.26, 15.69) * mm, "end": v(22.23, 15.72) * mm});
            skArc(sketch, "E15.15.20.0", {"start": v(22.82, 15.4) * mm, "mid": v(22.56, 15.63) * mm, "end": v(22.23, 15.72) * mm});
            skLineSegment(sketch, "E15.19.20.0", {"start": v(22.82, 15.4) * mm, "end": v(22.9, 15.3) * mm});
            skLineSegment(sketch, "E15.22.20.0", {"start": v(22.97, 15.19) * mm, "end": v(22.9, 15.3) * mm});
            skArc(sketch, "E15.25.20.0", {"start": v(23.03, 14.52) * mm, "mid": v(23.07, 14.86) * mm, "end": v(22.97, 15.19) * mm});
            skArc(sketch, "E15.29.20.0", {"start": v(22.1, 12.83) * mm, "mid": v(22.63, 13.64) * mm, "end": v(23.03, 14.52) * mm});
            skArc(sketch, "E15.33.20.0", {"start": v(21.87, 12.62) * mm, "mid": v(22, 12.71) * mm, "end": v(22.1, 12.83) * mm});
            skLineSegment(sketch, "E15.37.20.0", {"start": v(21.87, 12.62) * mm, "end": v(20.84, 12.03) * mm});
            skArc(sketch, "E15.40.20.0", {"start": v(20.84, 12.03) * mm, "mid": v(20.47, 11.56) * mm, "end": v(20.54, 10.97) * mm});
            skArc(sketch, "E15.2.21.0", {"start": v(13.56, 18.93) * mm, "mid": v(14.14, 18.79) * mm, "end": v(14.65, 19.1) * mm});
            skLineSegment(sketch, "E15.4.21.0", {"start": v(15.37, 20.03) * mm, "end": v(14.65, 19.1) * mm});
            skArc(sketch, "E15.7.21.0", {"start": v(15.6, 20.23) * mm, "mid": v(15.48, 20.14) * mm, "end": v(15.37, 20.03) * mm});
            skArc(sketch, "E15.11.21.0", {"start": v(15.6, 20.23) * mm, "mid": v(16.48, 20.65) * mm, "end": v(17.4, 20.93) * mm});
            skArc(sketch, "E15.15.21.0", {"start": v(18.06, 20.79) * mm, "mid": v(17.75, 20.93) * mm, "end": v(17.4, 20.93) * mm});
            skLineSegment(sketch, "E15.19.21.0", {"start": v(18.06, 20.79) * mm, "end": v(18.16, 20.7) * mm});
            skLineSegment(sketch, "E15.22.21.0", {"start": v(18.25, 20.62) * mm, "end": v(18.16, 20.7) * mm});
            skArc(sketch, "E15.25.21.0", {"start": v(18.48, 19.99) * mm, "mid": v(18.44, 20.33) * mm, "end": v(18.25, 20.62) * mm});
            skArc(sketch, "E15.29.21.0", {"start": v(18.02, 18.11) * mm, "mid": v(18.33, 19.03) * mm, "end": v(18.48, 19.99) * mm});
            skArc(sketch, "E15.33.21.0", {"start": v(17.85, 17.85) * mm, "mid": v(17.95, 17.97) * mm, "end": v(18.02, 18.11) * mm});
            skLineSegment(sketch, "E15.37.21.0", {"start": v(17.85, 17.85) * mm, "end": v(17.02, 17.02) * mm});
            skArc(sketch, "E15.40.21.0", {"start": v(17.02, 17.02) * mm, "mid": v(16.78, 16.47) * mm, "end": v(17, 15.91) * mm});
            skArc(sketch, "E15.2.22.0", {"start": v(8.2, 21.8) * mm, "mid": v(8.8, 21.8) * mm, "end": v(9.2, 22.23) * mm});
            skLineSegment(sketch, "E15.4.22.0", {"start": v(9.66, 23.33) * mm, "end": v(9.2, 22.23) * mm});
            skArc(sketch, "E15.7.22.0", {"start": v(9.83, 23.58) * mm, "mid": v(9.74, 23.46) * mm, "end": v(9.66, 23.33) * mm});
            skArc(sketch, "E15.11.22.0", {"start": v(9.83, 23.58) * mm, "mid": v(10.57, 24.21) * mm, "end": v(11.4, 24.72) * mm});
            skArc(sketch, "E15.15.22.0", {"start": v(12.06, 24.75) * mm, "mid": v(11.72, 24.81) * mm, "end": v(11.4, 24.72) * mm});
            skLineSegment(sketch, "E15.19.22.0", {"start": v(12.06, 24.75) * mm, "end": v(12.18, 24.7) * mm});
            skLineSegment(sketch, "E15.22.22.0", {"start": v(12.3, 24.64) * mm, "end": v(12.18, 24.7) * mm});
            skArc(sketch, "E15.25.22.0", {"start": v(12.68, 24.09) * mm, "mid": v(12.55, 24.4) * mm, "end": v(12.3, 24.64) * mm});
            skArc(sketch, "E15.29.22.0", {"start": v(12.72, 22.16) * mm, "mid": v(12.78, 23.12) * mm, "end": v(12.68, 24.09) * mm});
            skArc(sketch, "E15.33.22.0", {"start": v(12.62, 21.87) * mm, "mid": v(12.69, 22) * mm, "end": v(12.72, 22.16) * mm});
            skLineSegment(sketch, "E15.37.22.0", {"start": v(12.62, 21.87) * mm, "end": v(12.03, 20.84) * mm});
            skArc(sketch, "E15.40.22.0", {"start": v(12.03, 20.84) * mm, "mid": v(11.95, 20.25) * mm, "end": v(12.3, 19.77) * mm});
            skArc(sketch, "E15.2.23.0", {"start": v(2.28, 23.17) * mm, "mid": v(2.85, 23.34) * mm, "end": v(3.14, 23.86) * mm});
            skLineSegment(sketch, "E15.4.23.0", {"start": v(3.3, 25.03) * mm, "end": v(3.14, 23.86) * mm});
            skArc(sketch, "E15.7.23.0", {"start": v(3.4, 25.32) * mm, "mid": v(3.33, 25.18) * mm, "end": v(3.3, 25.03) * mm});
            skArc(sketch, "E15.11.23.0", {"start": v(3.4, 25.32) * mm, "mid": v(3.94, 26.12) * mm, "end": v(4.6, 26.83) * mm});
            skArc(sketch, "E15.15.23.0", {"start": v(5.24, 27.03) * mm, "mid": v(4.9, 27) * mm, "end": v(4.6, 26.83) * mm});
            skLineSegment(sketch, "E15.19.23.0", {"start": v(5.24, 27.03) * mm, "end": v(5.37, 27.01) * mm});
            skLineSegment(sketch, "E15.22.23.0", {"start": v(5.5, 26.98) * mm, "end": v(5.37, 27.01) * mm});
            skArc(sketch, "E15.25.23.0", {"start": v(6.01, 26.55) * mm, "mid": v(5.8, 26.82) * mm, "end": v(5.5, 26.98) * mm});
            skArc(sketch, "E15.29.23.0", {"start": v(6.55, 24.7) * mm, "mid": v(6.36, 25.64) * mm, "end": v(6.01, 26.55) * mm});
            skArc(sketch, "E15.33.23.0", {"start": v(6.53, 24.39) * mm, "mid": v(6.56, 24.54) * mm, "end": v(6.55, 24.7) * mm});
            skLineSegment(sketch, "E15.37.23.0", {"start": v(6.53, 24.39) * mm, "end": v(6.23, 23.24) * mm});
            skArc(sketch, "E15.40.23.0", {"start": v(6.23, 23.24) * mm, "mid": v(6.3, 22.65) * mm, "end": v(6.76, 22.28) * mm});
            skArc(sketch, "E16.trimOffspring", {"start": v(2.28, 23.17) * mm, "mid": v(1.52, 23.23) * mm, "end": v(0.77, 23.27) * mm});
            skArc(sketch, "E17.trimOffspring", {"start": v(8.2, 21.8) * mm, "mid": v(7.48, 22.05) * mm, "end": v(6.76, 22.28) * mm});
            skArc(sketch, "E18.trimOffspring", {"start": v(13.56, 18.93) * mm, "mid": v(12.94, 19.36) * mm, "end": v(12.3, 19.77) * mm});
            skArc(sketch, "E19.trimOffspring", {"start": v(18, 14.78) * mm, "mid": v(17.5, 15.35) * mm, "end": v(17, 15.91) * mm});
            skArc(sketch, "E20.trimOffspring", {"start": v(21.2, 9.61) * mm, "mid": v(20.88, 10.3) * mm, "end": v(20.54, 10.97) * mm});
            skArc(sketch, "E21.trimOffspring", {"start": v(22.97, 3.8) * mm, "mid": v(22.84, 4.54) * mm, "end": v(22.68, 5.28) * mm});
            skArc(sketch, "E22.trimOffspring", {"start": v(23.17, -2.28) * mm, "mid": v(23.23, -1.52) * mm, "end": v(23.27, -0.77) * mm});
            skArc(sketch, "E23.trimOffspring", {"start": v(21.8, -8.2) * mm, "mid": v(22.05, -7.48) * mm, "end": v(22.28, -6.76) * mm});
            skArc(sketch, "E24.trimOffspring", {"start": v(18.93, -13.56) * mm, "mid": v(19.36, -12.94) * mm, "end": v(19.77, -12.3) * mm});
            skArc(sketch, "E25.trimOffspring", {"start": v(14.78, -18) * mm, "mid": v(15.35, -17.5) * mm, "end": v(15.91, -17) * mm});
            skArc(sketch, "E26.trimOffspring", {"start": v(9.61, -21.2) * mm, "mid": v(10.3, -20.88) * mm, "end": v(10.97, -20.54) * mm});
            skArc(sketch, "E27.trimOffspring", {"start": v(3.8, -22.97) * mm, "mid": v(4.54, -22.84) * mm, "end": v(5.28, -22.68) * mm});
            skArc(sketch, "E28.trimOffspring", {"start": v(-2.28, -23.17) * mm, "mid": v(-1.52, -23.23) * mm, "end": v(-0.77, -23.27) * mm});
            skArc(sketch, "E29.trimOffspring", {"start": v(-8.2, -21.8) * mm, "mid": v(-7.48, -22.05) * mm, "end": v(-6.76, -22.28) * mm});
            skArc(sketch, "E30.trimOffspring", {"start": v(-13.56, -18.93) * mm, "mid": v(-12.94, -19.36) * mm, "end": v(-12.3, -19.77) * mm});
            skArc(sketch, "E31.trimOffspring", {"start": v(-18, -14.78) * mm, "mid": v(-17.5, -15.35) * mm, "end": v(-17, -15.91) * mm});
            skArc(sketch, "E32.trimOffspring", {"start": v(-21.2, -9.61) * mm, "mid": v(-20.88, -10.3) * mm, "end": v(-20.54, -10.97) * mm});
            skArc(sketch, "E33.trimOffspring", {"start": v(-22.97, -3.8) * mm, "mid": v(-22.84, -4.54) * mm, "end": v(-22.68, -5.28) * mm});
            skArc(sketch, "E34.trimOffspring", {"start": v(-23.17, 2.28) * mm, "mid": v(-23.23, 1.52) * mm, "end": v(-23.27, 0.77) * mm});
            skArc(sketch, "E35.trimOffspring", {"start": v(-21.8, 8.2) * mm, "mid": v(-22.05, 7.48) * mm, "end": v(-22.28, 6.76) * mm});
            skArc(sketch, "E36.trimOffspring", {"start": v(-18.93, 13.56) * mm, "mid": v(-19.36, 12.94) * mm, "end": v(-19.77, 12.3) * mm});
            skArc(sketch, "E37.trimOffspring", {"start": v(-14.78, 18) * mm, "mid": v(-15.35, 17.5) * mm, "end": v(-15.91, 17) * mm});
            skArc(sketch, "E38.trimOffspring", {"start": v(-9.61, 21.2) * mm, "mid": v(-10.3, 20.88) * mm, "end": v(-10.97, 20.54) * mm});
            skSolve(sketch);
        }
        {
            var Q0;
            Q0=qSketchRegion(id+"F0",true);
            var Q1;
            Q1=makeQuery(id+"F0.imprint","IMPRINT",FACE,{"disambiguationData":[TD([[makeQuery(id+"F0.imprint","IMPRINT",EDGE,{"derivedFrom":sQuery(id+"F0.wireOp",EDGE,"E0")}),1.0]])]});
            extrude(context, id + "F1", {"entities" : qUnion([Q0, Q1]), "depth" : 6.35 * mm});
        }
        {
            var Q0;
            Q0=makeQuery(id+"F1.opExtrude","CAP_FACE",FACE,{"disambiguationData":[OSD([sQuery(id+"F0.wireOp",EDGE,"E0"),sQuery(id+"F0.wireOp",EDGE,"E1.trimOffspring"),sQuery(id+"F0.wireOp",EDGE,"E2"),sQuery(id+"F0.wireOp",EDGE,"E3"),sQuery(id+"F0.wireOp",EDGE,"E4.MirrorCS"),sQuery(id+"F0.wireOp",EDGE,"E5.MirrorCS"),sQuery(id+"F0.wireOp",EDGE,"E6.MirrorCS"),sQuery(id+"F0.wireOp",EDGE,"E8.filletArc"),sQuery(id+"F0.wireOp",EDGE,"E9.filletArc"),sQuery(id+"F0.wireOp",EDGE,"E10.filletArc"),sQuery(id+"F0.wireOp",EDGE,"E11.filletArc"),sQuery(id+"F0.wireOp",EDGE,"E12.filletArc"),sQuery(id+"F0.wireOp",EDGE,"E13.filletArc"),sQuery(id+"F0.wireOp",EDGE,"E14.1.0"),sQuery(id+"F0.wireOp",EDGE,"E14.1.1"),sQuery(id+"F0.wireOp",EDGE,"E14.1.2"),sQuery(id+"F0.wireOp",EDGE,"E14.1.3"),sQuery(id+"F0.wireOp",EDGE,"E14.1.4"),sQuery(id+"F0.wireOp",EDGE,"E14.1.5"),sQuery(id+"F0.wireOp",EDGE,"E14.1.6"),sQuery(id+"F0.wireOp",EDGE,"E14.1.7"),sQuery(id+"F0.wireOp",EDGE,"E14.1.8"),sQuery(id+"F0.wireOp",EDGE,"E14.1.9"),sQuery(id+"F0.wireOp",EDGE,"E14.1.10"),sQuery(id+"F0.wireOp",EDGE,"E14.1.11"),sQuery(id+"F0.wireOp",EDGE,"E14.2.0"),sQuery(id+"F0.wireOp",EDGE,"E14.2.1"),sQuery(id+"F0.wireOp",EDGE,"E14.2.2"),sQuery(id+"F0.wireOp",EDGE,"E14.2.3"),sQuery(id+"F0.wireOp",EDGE,"E14.2.4"),sQuery(id+"F0.wireOp",EDGE,"E14.2.5"),sQuery(id+"F0.wireOp",EDGE,"E14.2.6"),sQuery(id+"F0.wireOp",EDGE,"E14.2.7"),sQuery(id+"F0.wireOp",EDGE,"E14.2.8"),sQuery(id+"F0.wireOp",EDGE,"E14.2.9"),sQuery(id+"F0.wireOp",EDGE,"E14.2.10"),sQuery(id+"F0.wireOp",EDGE,"E14.2.11"),sQuery(id+"F0.wireOp",EDGE,"E15.2.3.0"),sQuery(id+"F0.wireOp",EDGE,"E15.4.3.0"),sQuery(id+"F0.wireOp",EDGE,"E15.7.3.0"),sQuery(id+"F0.wireOp",EDGE,"E15.11.3.0"),sQuery(id+"F0.wireOp",EDGE,"E15.15.3.0"),sQuery(id+"F0.wireOp",EDGE,"E15.19.3.0"),sQuery(id+"F0.wireOp",EDGE,"E15.22.3.0"),sQuery(id+"F0.wireOp",EDGE,"E15.25.3.0"),sQuery(id+"F0.wireOp",EDGE,"E15.29.3.0"),sQuery(id+"F0.wireOp",EDGE,"E15.33.3.0"),sQuery(id+"F0.wireOp",EDGE,"E15.37.3.0"),sQuery(id+"F0.wireOp",EDGE,"E15.40.3.0"),sQuery(id+"F0.wireOp",EDGE,"E15.2.4.0"),sQuery(id+"F0.wireOp",EDGE,"E15.4.4.0"),sQuery(id+"F0.wireOp",EDGE,"E15.7.4.0"),sQuery(id+"F0.wireOp",EDGE,"E15.11.4.0"),sQuery(id+"F0.wireOp",EDGE,"E15.15.4.0"),sQuery(id+"F0.wireOp",EDGE,"E15.19.4.0"),sQuery(id+"F0.wireOp",EDGE,"E15.22.4.0"),sQuery(id+"F0.wireOp",EDGE,"E15.25.4.0"),sQuery(id+"F0.wireOp",EDGE,"E15.29.4.0"),sQuery(id+"F0.wireOp",EDGE,"E15.33.4.0"),sQuery(id+"F0.wireOp",EDGE,"E15.37.4.0"),sQuery(id+"F0.wireOp",EDGE,"E15.40.4.0"),sQuery(id+"F0.wireOp",EDGE,"E15.2.5.0"),sQuery(id+"F0.wireOp",EDGE,"E15.4.5.0"),sQuery(id+"F0.wireOp",EDGE,"E15.7.5.0"),sQuery(id+"F0.wireOp",EDGE,"E15.11.5.0"),sQuery(id+"F0.wireOp",EDGE,"E15.15.5.0"),sQuery(id+"F0.wireOp",EDGE,"E15.19.5.0"),sQuery(id+"F0.wireOp",EDGE,"E15.22.5.0"),sQuery(id+"F0.wireOp",EDGE,"E15.25.5.0"),sQuery(id+"F0.wireOp",EDGE,"E15.29.5.0"),sQuery(id+"F0.wireOp",EDGE,"E15.33.5.0"),sQuery(id+"F0.wireOp",EDGE,"E15.37.5.0"),sQuery(id+"F0.wireOp",EDGE,"E15.40.5.0"),sQuery(id+"F0.wireOp",EDGE,"E15.2.6.0"),sQuery(id+"F0.wireOp",EDGE,"E15.4.6.0"),sQuery(id+"F0.wireOp",EDGE,"E15.7.6.0"),sQuery(id+"F0.wireOp",EDGE,"E15.11.6.0"),sQuery(id+"F0.wireOp",EDGE,"E15.15.6.0"),sQuery(id+"F0.wireOp",EDGE,"E15.19.6.0"),sQuery(id+"F0.wireOp",EDGE,"E15.22.6.0"),sQuery(id+"F0.wireOp",EDGE,"E15.25.6.0"),sQuery(id+"F0.wireOp",EDGE,"E15.29.6.0"),sQuery(id+"F0.wireOp",EDGE,"E15.33.6.0"),sQuery(id+"F0.wireOp",EDGE,"E15.37.6.0"),sQuery(id+"F0.wireOp",EDGE,"E15.40.6.0"),sQuery(id+"F0.wireOp",EDGE,"E15.2.7.0"),sQuery(id+"F0.wireOp",EDGE,"E15.4.7.0"),sQuery(id+"F0.wireOp",EDGE,"E15.7.7.0"),sQuery(id+"F0.wireOp",EDGE,"E15.11.7.0"),sQuery(id+"F0.wireOp",EDGE,"E15.15.7.0"),sQuery(id+"F0.wireOp",EDGE,"E15.19.7.0"),sQuery(id+"F0.wireOp",EDGE,"E15.22.7.0"),sQuery(id+"F0.wireOp",EDGE,"E15.25.7.0"),sQuery(id+"F0.wireOp",EDGE,"E15.29.7.0"),sQuery(id+"F0.wireOp",EDGE,"E15.33.7.0"),sQuery(id+"F0.wireOp",EDGE,"E15.37.7.0"),sQuery(id+"F0.wireOp",EDGE,"E15.40.7.0"),sQuery(id+"F0.wireOp",EDGE,"E15.2.8.0"),sQuery(id+"F0.wireOp",EDGE,"E15.4.8.0"),sQuery(id+"F0.wireOp",EDGE,"E15.7.8.0"),sQuery(id+"F0.wireOp",EDGE,"E15.11.8.0"),sQuery(id+"F0.wireOp",EDGE,"E15.15.8.0"),sQuery(id+"F0.wireOp",EDGE,"E15.19.8.0"),sQuery(id+"F0.wireOp",EDGE,"E15.22.8.0"),sQuery(id+"F0.wireOp",EDGE,"E15.25.8.0"),sQuery(id+"F0.wireOp",EDGE,"E15.29.8.0"),sQuery(id+"F0.wireOp",EDGE,"E15.33.8.0"),sQuery(id+"F0.wireOp",EDGE,"E15.37.8.0"),sQuery(id+"F0.wireOp",EDGE,"E15.40.8.0"),sQuery(id+"F0.wireOp",EDGE,"E15.2.9.0"),sQuery(id+"F0.wireOp",EDGE,"E15.4.9.0"),sQuery(id+"F0.wireOp",EDGE,"E15.7.9.0"),sQuery(id+"F0.wireOp",EDGE,"E15.11.9.0"),sQuery(id+"F0.wireOp",EDGE,"E15.15.9.0"),sQuery(id+"F0.wireOp",EDGE,"E15.19.9.0"),sQuery(id+"F0.wireOp",EDGE,"E15.22.9.0"),sQuery(id+"F0.wireOp",EDGE,"E15.25.9.0"),sQuery(id+"F0.wireOp",EDGE,"E15.29.9.0"),sQuery(id+"F0.wireOp",EDGE,"E15.33.9.0"),sQuery(id+"F0.wireOp",EDGE,"E15.37.9.0"),sQuery(id+"F0.wireOp",EDGE,"E15.40.9.0"),sQuery(id+"F0.wireOp",EDGE,"E15.2.10.0"),sQuery(id+"F0.wireOp",EDGE,"E15.4.10.0"),sQuery(id+"F0.wireOp",EDGE,"E15.7.10.0"),sQuery(id+"F0.wireOp",EDGE,"E15.11.10.0"),sQuery(id+"F0.wireOp",EDGE,"E15.15.10.0"),sQuery(id+"F0.wireOp",EDGE,"E15.19.10.0"),sQuery(id+"F0.wireOp",EDGE,"E15.22.10.0"),sQuery(id+"F0.wireOp",EDGE,"E15.25.10.0"),sQuery(id+"F0.wireOp",EDGE,"E15.29.10.0"),sQuery(id+"F0.wireOp",EDGE,"E15.33.10.0"),sQuery(id+"F0.wireOp",EDGE,"E15.37.10.0"),sQuery(id+"F0.wireOp",EDGE,"E15.40.10.0"),sQuery(id+"F0.wireOp",EDGE,"E15.2.11.0"),sQuery(id+"F0.wireOp",EDGE,"E15.4.11.0"),sQuery(id+"F0.wireOp",EDGE,"E15.7.11.0"),sQuery(id+"F0.wireOp",EDGE,"E15.11.11.0"),sQuery(id+"F0.wireOp",EDGE,"E15.15.11.0"),sQuery(id+"F0.wireOp",EDGE,"E15.19.11.0"),sQuery(id+"F0.wireOp",EDGE,"E15.22.11.0"),sQuery(id+"F0.wireOp",EDGE,"E15.25.11.0"),sQuery(id+"F0.wireOp",EDGE,"E15.29.11.0"),sQuery(id+"F0.wireOp",EDGE,"E15.33.11.0"),sQuery(id+"F0.wireOp",EDGE,"E15.37.11.0"),sQuery(id+"F0.wireOp",EDGE,"E15.40.11.0"),sQuery(id+"F0.wireOp",EDGE,"E15.2.12.0"),sQuery(id+"F0.wireOp",EDGE,"E15.4.12.0"),sQuery(id+"F0.wireOp",EDGE,"E15.7.12.0"),sQuery(id+"F0.wireOp",EDGE,"E15.11.12.0"),sQuery(id+"F0.wireOp",EDGE,"E15.15.12.0"),sQuery(id+"F0.wireOp",EDGE,"E15.19.12.0"),sQuery(id+"F0.wireOp",EDGE,"E15.22.12.0"),sQuery(id+"F0.wireOp",EDGE,"E15.25.12.0"),sQuery(id+"F0.wireOp",EDGE,"E15.29.12.0"),sQuery(id+"F0.wireOp",EDGE,"E15.33.12.0"),sQuery(id+"F0.wireOp",EDGE,"E15.37.12.0"),sQuery(id+"F0.wireOp",EDGE,"E15.40.12.0"),sQuery(id+"F0.wireOp",EDGE,"E15.2.13.0"),sQuery(id+"F0.wireOp",EDGE,"E15.4.13.0"),sQuery(id+"F0.wireOp",EDGE,"E15.7.13.0"),sQuery(id+"F0.wireOp",EDGE,"E15.11.13.0"),sQuery(id+"F0.wireOp",EDGE,"E15.15.13.0"),sQuery(id+"F0.wireOp",EDGE,"E15.19.13.0"),sQuery(id+"F0.wireOp",EDGE,"E15.22.13.0"),sQuery(id+"F0.wireOp",EDGE,"E15.25.13.0"),sQuery(id+"F0.wireOp",EDGE,"E15.29.13.0"),sQuery(id+"F0.wireOp",EDGE,"E15.33.13.0"),sQuery(id+"F0.wireOp",EDGE,"E15.37.13.0"),sQuery(id+"F0.wireOp",EDGE,"E15.40.13.0"),sQuery(id+"F0.wireOp",EDGE,"E15.2.14.0"),sQuery(id+"F0.wireOp",EDGE,"E15.4.14.0"),sQuery(id+"F0.wireOp",EDGE,"E15.7.14.0"),sQuery(id+"F0.wireOp",EDGE,"E15.11.14.0"),sQuery(id+"F0.wireOp",EDGE,"E15.15.14.0"),sQuery(id+"F0.wireOp",EDGE,"E15.19.14.0"),sQuery(id+"F0.wireOp",EDGE,"E15.22.14.0"),sQuery(id+"F0.wireOp",EDGE,"E15.25.14.0"),sQuery(id+"F0.wireOp",EDGE,"E15.29.14.0"),sQuery(id+"F0.wireOp",EDGE,"E15.33.14.0"),sQuery(id+"F0.wireOp",EDGE,"E15.37.14.0"),sQuery(id+"F0.wireOp",EDGE,"E15.40.14.0"),sQuery(id+"F0.wireOp",EDGE,"E15.2.15.0"),sQuery(id+"F0.wireOp",EDGE,"E15.4.15.0"),sQuery(id+"F0.wireOp",EDGE,"E15.7.15.0"),sQuery(id+"F0.wireOp",EDGE,"E15.11.15.0"),sQuery(id+"F0.wireOp",EDGE,"E15.15.15.0"),sQuery(id+"F0.wireOp",EDGE,"E15.19.15.0"),sQuery(id+"F0.wireOp",EDGE,"E15.22.15.0"),sQuery(id+"F0.wireOp",EDGE,"E15.25.15.0"),sQuery(id+"F0.wireOp",EDGE,"E15.29.15.0"),sQuery(id+"F0.wireOp",EDGE,"E15.33.15.0"),sQuery(id+"F0.wireOp",EDGE,"E15.37.15.0"),sQuery(id+"F0.wireOp",EDGE,"E15.40.15.0"),sQuery(id+"F0.wireOp",EDGE,"E15.2.16.0"),sQuery(id+"F0.wireOp",EDGE,"E15.4.16.0"),sQuery(id+"F0.wireOp",EDGE,"E15.7.16.0"),sQuery(id+"F0.wireOp",EDGE,"E15.11.16.0"),sQuery(id+"F0.wireOp",EDGE,"E15.15.16.0"),sQuery(id+"F0.wireOp",EDGE,"E15.19.16.0"),sQuery(id+"F0.wireOp",EDGE,"E15.22.16.0"),sQuery(id+"F0.wireOp",EDGE,"E15.25.16.0"),sQuery(id+"F0.wireOp",EDGE,"E15.29.16.0"),sQuery(id+"F0.wireOp",EDGE,"E15.33.16.0"),sQuery(id+"F0.wireOp",EDGE,"E15.37.16.0"),sQuery(id+"F0.wireOp",EDGE,"E15.40.16.0"),sQuery(id+"F0.wireOp",EDGE,"E15.2.17.0"),sQuery(id+"F0.wireOp",EDGE,"E15.4.17.0"),sQuery(id+"F0.wireOp",EDGE,"E15.7.17.0"),sQuery(id+"F0.wireOp",EDGE,"E15.11.17.0"),sQuery(id+"F0.wireOp",EDGE,"E15.15.17.0"),sQuery(id+"F0.wireOp",EDGE,"E15.19.17.0"),sQuery(id+"F0.wireOp",EDGE,"E15.22.17.0"),sQuery(id+"F0.wireOp",EDGE,"E15.25.17.0"),sQuery(id+"F0.wireOp",EDGE,"E15.29.17.0"),sQuery(id+"F0.wireOp",EDGE,"E15.33.17.0"),sQuery(id+"F0.wireOp",EDGE,"E15.37.17.0"),sQuery(id+"F0.wireOp",EDGE,"E15.40.17.0"),sQuery(id+"F0.wireOp",EDGE,"E15.2.18.0"),sQuery(id+"F0.wireOp",EDGE,"E15.4.18.0"),sQuery(id+"F0.wireOp",EDGE,"E15.7.18.0"),sQuery(id+"F0.wireOp",EDGE,"E15.11.18.0"),sQuery(id+"F0.wireOp",EDGE,"E15.15.18.0"),sQuery(id+"F0.wireOp",EDGE,"E15.19.18.0"),sQuery(id+"F0.wireOp",EDGE,"E15.22.18.0"),sQuery(id+"F0.wireOp",EDGE,"E15.25.18.0"),sQuery(id+"F0.wireOp",EDGE,"E15.29.18.0"),sQuery(id+"F0.wireOp",EDGE,"E15.33.18.0"),sQuery(id+"F0.wireOp",EDGE,"E15.37.18.0"),sQuery(id+"F0.wireOp",EDGE,"E15.40.18.0"),sQuery(id+"F0.wireOp",EDGE,"E15.2.19.0"),sQuery(id+"F0.wireOp",EDGE,"E15.4.19.0"),sQuery(id+"F0.wireOp",EDGE,"E15.7.19.0"),sQuery(id+"F0.wireOp",EDGE,"E15.11.19.0"),sQuery(id+"F0.wireOp",EDGE,"E15.15.19.0"),sQuery(id+"F0.wireOp",EDGE,"E15.19.19.0"),sQuery(id+"F0.wireOp",EDGE,"E15.22.19.0"),sQuery(id+"F0.wireOp",EDGE,"E15.25.19.0"),sQuery(id+"F0.wireOp",EDGE,"E15.29.19.0"),sQuery(id+"F0.wireOp",EDGE,"E15.33.19.0"),sQuery(id+"F0.wireOp",EDGE,"E15.37.19.0"),sQuery(id+"F0.wireOp",EDGE,"E15.40.19.0"),sQuery(id+"F0.wireOp",EDGE,"E15.2.20.0"),sQuery(id+"F0.wireOp",EDGE,"E15.4.20.0"),sQuery(id+"F0.wireOp",EDGE,"E15.7.20.0"),sQuery(id+"F0.wireOp",EDGE,"E15.11.20.0"),sQuery(id+"F0.wireOp",EDGE,"E15.15.20.0"),sQuery(id+"F0.wireOp",EDGE,"E15.19.20.0"),sQuery(id+"F0.wireOp",EDGE,"E15.22.20.0"),sQuery(id+"F0.wireOp",EDGE,"E15.25.20.0"),sQuery(id+"F0.wireOp",EDGE,"E15.29.20.0"),sQuery(id+"F0.wireOp",EDGE,"E15.33.20.0"),sQuery(id+"F0.wireOp",EDGE,"E15.37.20.0"),sQuery(id+"F0.wireOp",EDGE,"E15.40.20.0"),sQuery(id+"F0.wireOp",EDGE,"E15.2.21.0"),sQuery(id+"F0.wireOp",EDGE,"E15.4.21.0"),sQuery(id+"F0.wireOp",EDGE,"E15.7.21.0"),sQuery(id+"F0.wireOp",EDGE,"E15.11.21.0"),sQuery(id+"F0.wireOp",EDGE,"E15.15.21.0"),sQuery(id+"F0.wireOp",EDGE,"E15.19.21.0"),sQuery(id+"F0.wireOp",EDGE,"E15.22.21.0"),sQuery(id+"F0.wireOp",EDGE,"E15.25.21.0"),sQuery(id+"F0.wireOp",EDGE,"E15.29.21.0"),sQuery(id+"F0.wireOp",EDGE,"E15.33.21.0"),sQuery(id+"F0.wireOp",EDGE,"E15.37.21.0"),sQuery(id+"F0.wireOp",EDGE,"E15.40.21.0"),sQuery(id+"F0.wireOp",EDGE,"E15.2.22.0"),sQuery(id+"F0.wireOp",EDGE,"E15.4.22.0"),sQuery(id+"F0.wireOp",EDGE,"E15.7.22.0"),sQuery(id+"F0.wireOp",EDGE,"E15.11.22.0"),sQuery(id+"F0.wireOp",EDGE,"E15.15.22.0"),sQuery(id+"F0.wireOp",EDGE,"E15.19.22.0"),sQuery(id+"F0.wireOp",EDGE,"E15.22.22.0"),sQuery(id+"F0.wireOp",EDGE,"E15.25.22.0"),sQuery(id+"F0.wireOp",EDGE,"E15.29.22.0"),sQuery(id+"F0.wireOp",EDGE,"E15.33.22.0"),sQuery(id+"F0.wireOp",EDGE,"E15.37.22.0"),sQuery(id+"F0.wireOp",EDGE,"E15.40.22.0"),sQuery(id+"F0.wireOp",EDGE,"E15.2.23.0"),sQuery(id+"F0.wireOp",EDGE,"E15.4.23.0"),sQuery(id+"F0.wireOp",EDGE,"E15.7.23.0"),sQuery(id+"F0.wireOp",EDGE,"E15.11.23.0"),sQuery(id+"F0.wireOp",EDGE,"E15.15.23.0"),sQuery(id+"F0.wireOp",EDGE,"E15.19.23.0"),sQuery(id+"F0.wireOp",EDGE,"E15.22.23.0"),sQuery(id+"F0.wireOp",EDGE,"E15.25.23.0"),sQuery(id+"F0.wireOp",EDGE,"E15.29.23.0"),sQuery(id+"F0.wireOp",EDGE,"E15.33.23.0"),sQuery(id+"F0.wireOp",EDGE,"E15.37.23.0"),sQuery(id+"F0.wireOp",EDGE,"E15.40.23.0"),sQuery(id+"F0.wireOp",EDGE,"E16.trimOffspring"),sQuery(id+"F0.wireOp",EDGE,"E17.trimOffspring"),sQuery(id+"F0.wireOp",EDGE,"E18.trimOffspring"),sQuery(id+"F0.wireOp",EDGE,"E19.trimOffspring"),sQuery(id+"F0.wireOp",EDGE,"E20.trimOffspring"),sQuery(id+"F0.wireOp",EDGE,"E21.trimOffspring"),sQuery(id+"F0.wireOp",EDGE,"E22.trimOffspring"),sQuery(id+"F0.wireOp",EDGE,"E23.trimOffspring"),sQuery(id+"F0.wireOp",EDGE,"E24.trimOffspring"),sQuery(id+"F0.wireOp",EDGE,"E25.trimOffspring"),sQuery(id+"F0.wireOp",EDGE,"E26.trimOffspring"),sQuery(id+"F0.wireOp",EDGE,"E27.trimOffspring"),sQuery(id+"F0.wireOp",EDGE,"E28.trimOffspring"),sQuery(id+"F0.wireOp",EDGE,"E29.trimOffspring"),sQuery(id+"F0.wireOp",EDGE,"E30.trimOffspring"),sQuery(id+"F0.wireOp",EDGE,"E31.trimOffspring"),sQuery(id+"F0.wireOp",EDGE,"E32.trimOffspring"),sQuery(id+"F0.wireOp",EDGE,"E33.trimOffspring"),sQuery(id+"F0.wireOp",EDGE,"E34.trimOffspring"),sQuery(id+"F0.wireOp",EDGE,"E35.trimOffspring"),sQuery(id+"F0.wireOp",EDGE,"E36.trimOffspring"),sQuery(id+"F0.wireOp",EDGE,"E37.trimOffspring"),sQuery(id+"F0.wireOp",EDGE,"E38.trimOffspring")])],"isStart":false});
            var sketch = newSketch(context, id + "F2", { "sketchPlane" : qUnion([Q0])});
            skCircle(sketch, "E39", {"center": v(0, 0) * mm, "radius": 6.35 * mm});
            skSolve(sketch);
        }
        {
            var Q0;
            Q0=qSketchRegion(id+"F2",true);
            extrude(context, id + "F3", {"entities" : qUnion([Q0]), "operationType" : NewBodyOperationType.ADD, "depth" : 19.05 * mm});
        }
        {
            var Q0;
            Q0=makeQuery(id+"F1.opExtrude","CAP_FACE",FACE,{"disambiguationData":[OSD([sQuery(id+"F0.wireOp",EDGE,"E0"),sQuery(id+"F0.wireOp",EDGE,"E1.trimOffspring"),sQuery(id+"F0.wireOp",EDGE,"E2"),sQuery(id+"F0.wireOp",EDGE,"E3"),sQuery(id+"F0.wireOp",EDGE,"E4.MirrorCS"),sQuery(id+"F0.wireOp",EDGE,"E5.MirrorCS"),sQuery(id+"F0.wireOp",EDGE,"E6.MirrorCS"),sQuery(id+"F0.wireOp",EDGE,"E8.filletArc"),sQuery(id+"F0.wireOp",EDGE,"E9.filletArc"),sQuery(id+"F0.wireOp",EDGE,"E10.filletArc"),sQuery(id+"F0.wireOp",EDGE,"E11.filletArc"),sQuery(id+"F0.wireOp",EDGE,"E12.filletArc"),sQuery(id+"F0.wireOp",EDGE,"E13.filletArc"),sQuery(id+"F0.wireOp",EDGE,"E14.1.0"),sQuery(id+"F0.wireOp",EDGE,"E14.1.1"),sQuery(id+"F0.wireOp",EDGE,"E14.1.2"),sQuery(id+"F0.wireOp",EDGE,"E14.1.3"),sQuery(id+"F0.wireOp",EDGE,"E14.1.4"),sQuery(id+"F0.wireOp",EDGE,"E14.1.5"),sQuery(id+"F0.wireOp",EDGE,"E14.1.6"),sQuery(id+"F0.wireOp",EDGE,"E14.1.7"),sQuery(id+"F0.wireOp",EDGE,"E14.1.8"),sQuery(id+"F0.wireOp",EDGE,"E14.1.9"),sQuery(id+"F0.wireOp",EDGE,"E14.1.10"),sQuery(id+"F0.wireOp",EDGE,"E14.1.11"),sQuery(id+"F0.wireOp",EDGE,"E14.2.0"),sQuery(id+"F0.wireOp",EDGE,"E14.2.1"),sQuery(id+"F0.wireOp",EDGE,"E14.2.2"),sQuery(id+"F0.wireOp",EDGE,"E14.2.3"),sQuery(id+"F0.wireOp",EDGE,"E14.2.4"),sQuery(id+"F0.wireOp",EDGE,"E14.2.5"),sQuery(id+"F0.wireOp",EDGE,"E14.2.6"),sQuery(id+"F0.wireOp",EDGE,"E14.2.7"),sQuery(id+"F0.wireOp",EDGE,"E14.2.8"),sQuery(id+"F0.wireOp",EDGE,"E14.2.9"),sQuery(id+"F0.wireOp",EDGE,"E14.2.10"),sQuery(id+"F0.wireOp",EDGE,"E14.2.11"),sQuery(id+"F0.wireOp",EDGE,"E15.2.3.0"),sQuery(id+"F0.wireOp",EDGE,"E15.4.3.0"),sQuery(id+"F0.wireOp",EDGE,"E15.7.3.0"),sQuery(id+"F0.wireOp",EDGE,"E15.11.3.0"),sQuery(id+"F0.wireOp",EDGE,"E15.15.3.0"),sQuery(id+"F0.wireOp",EDGE,"E15.19.3.0"),sQuery(id+"F0.wireOp",EDGE,"E15.22.3.0"),sQuery(id+"F0.wireOp",EDGE,"E15.25.3.0"),sQuery(id+"F0.wireOp",EDGE,"E15.29.3.0"),sQuery(id+"F0.wireOp",EDGE,"E15.33.3.0"),sQuery(id+"F0.wireOp",EDGE,"E15.37.3.0"),sQuery(id+"F0.wireOp",EDGE,"E15.40.3.0"),sQuery(id+"F0.wireOp",EDGE,"E15.2.4.0"),sQuery(id+"F0.wireOp",EDGE,"E15.4.4.0"),sQuery(id+"F0.wireOp",EDGE,"E15.7.4.0"),sQuery(id+"F0.wireOp",EDGE,"E15.11.4.0"),sQuery(id+"F0.wireOp",EDGE,"E15.15.4.0"),sQuery(id+"F0.wireOp",EDGE,"E15.19.4.0"),sQuery(id+"F0.wireOp",EDGE,"E15.22.4.0"),sQuery(id+"F0.wireOp",EDGE,"E15.25.4.0"),sQuery(id+"F0.wireOp",EDGE,"E15.29.4.0"),sQuery(id+"F0.wireOp",EDGE,"E15.33.4.0"),sQuery(id+"F0.wireOp",EDGE,"E15.37.4.0"),sQuery(id+"F0.wireOp",EDGE,"E15.40.4.0"),sQuery(id+"F0.wireOp",EDGE,"E15.2.5.0"),sQuery(id+"F0.wireOp",EDGE,"E15.4.5.0"),sQuery(id+"F0.wireOp",EDGE,"E15.7.5.0"),sQuery(id+"F0.wireOp",EDGE,"E15.11.5.0"),sQuery(id+"F0.wireOp",EDGE,"E15.15.5.0"),sQuery(id+"F0.wireOp",EDGE,"E15.19.5.0"),sQuery(id+"F0.wireOp",EDGE,"E15.22.5.0"),sQuery(id+"F0.wireOp",EDGE,"E15.25.5.0"),sQuery(id+"F0.wireOp",EDGE,"E15.29.5.0"),sQuery(id+"F0.wireOp",EDGE,"E15.33.5.0"),sQuery(id+"F0.wireOp",EDGE,"E15.37.5.0"),sQuery(id+"F0.wireOp",EDGE,"E15.40.5.0"),sQuery(id+"F0.wireOp",EDGE,"E15.2.6.0"),sQuery(id+"F0.wireOp",EDGE,"E15.4.6.0"),sQuery(id+"F0.wireOp",EDGE,"E15.7.6.0"),sQuery(id+"F0.wireOp",EDGE,"E15.11.6.0"),sQuery(id+"F0.wireOp",EDGE,"E15.15.6.0"),sQuery(id+"F0.wireOp",EDGE,"E15.19.6.0"),sQuery(id+"F0.wireOp",EDGE,"E15.22.6.0"),sQuery(id+"F0.wireOp",EDGE,"E15.25.6.0"),sQuery(id+"F0.wireOp",EDGE,"E15.29.6.0"),sQuery(id+"F0.wireOp",EDGE,"E15.33.6.0"),sQuery(id+"F0.wireOp",EDGE,"E15.37.6.0"),sQuery(id+"F0.wireOp",EDGE,"E15.40.6.0"),sQuery(id+"F0.wireOp",EDGE,"E15.2.7.0"),sQuery(id+"F0.wireOp",EDGE,"E15.4.7.0"),sQuery(id+"F0.wireOp",EDGE,"E15.7.7.0"),sQuery(id+"F0.wireOp",EDGE,"E15.11.7.0"),sQuery(id+"F0.wireOp",EDGE,"E15.15.7.0"),sQuery(id+"F0.wireOp",EDGE,"E15.19.7.0"),sQuery(id+"F0.wireOp",EDGE,"E15.22.7.0"),sQuery(id+"F0.wireOp",EDGE,"E15.25.7.0"),sQuery(id+"F0.wireOp",EDGE,"E15.29.7.0"),sQuery(id+"F0.wireOp",EDGE,"E15.33.7.0"),sQuery(id+"F0.wireOp",EDGE,"E15.37.7.0"),sQuery(id+"F0.wireOp",EDGE,"E15.40.7.0"),sQuery(id+"F0.wireOp",EDGE,"E15.2.8.0"),sQuery(id+"F0.wireOp",EDGE,"E15.4.8.0"),sQuery(id+"F0.wireOp",EDGE,"E15.7.8.0"),sQuery(id+"F0.wireOp",EDGE,"E15.11.8.0"),sQuery(id+"F0.wireOp",EDGE,"E15.15.8.0"),sQuery(id+"F0.wireOp",EDGE,"E15.19.8.0"),sQuery(id+"F0.wireOp",EDGE,"E15.22.8.0"),sQuery(id+"F0.wireOp",EDGE,"E15.25.8.0"),sQuery(id+"F0.wireOp",EDGE,"E15.29.8.0"),sQuery(id+"F0.wireOp",EDGE,"E15.33.8.0"),sQuery(id+"F0.wireOp",EDGE,"E15.37.8.0"),sQuery(id+"F0.wireOp",EDGE,"E15.40.8.0"),sQuery(id+"F0.wireOp",EDGE,"E15.2.9.0"),sQuery(id+"F0.wireOp",EDGE,"E15.4.9.0"),sQuery(id+"F0.wireOp",EDGE,"E15.7.9.0"),sQuery(id+"F0.wireOp",EDGE,"E15.11.9.0"),sQuery(id+"F0.wireOp",EDGE,"E15.15.9.0"),sQuery(id+"F0.wireOp",EDGE,"E15.19.9.0"),sQuery(id+"F0.wireOp",EDGE,"E15.22.9.0"),sQuery(id+"F0.wireOp",EDGE,"E15.25.9.0"),sQuery(id+"F0.wireOp",EDGE,"E15.29.9.0"),sQuery(id+"F0.wireOp",EDGE,"E15.33.9.0"),sQuery(id+"F0.wireOp",EDGE,"E15.37.9.0"),sQuery(id+"F0.wireOp",EDGE,"E15.40.9.0"),sQuery(id+"F0.wireOp",EDGE,"E15.2.10.0"),sQuery(id+"F0.wireOp",EDGE,"E15.4.10.0"),sQuery(id+"F0.wireOp",EDGE,"E15.7.10.0"),sQuery(id+"F0.wireOp",EDGE,"E15.11.10.0"),sQuery(id+"F0.wireOp",EDGE,"E15.15.10.0"),sQuery(id+"F0.wireOp",EDGE,"E15.19.10.0"),sQuery(id+"F0.wireOp",EDGE,"E15.22.10.0"),sQuery(id+"F0.wireOp",EDGE,"E15.25.10.0"),sQuery(id+"F0.wireOp",EDGE,"E15.29.10.0"),sQuery(id+"F0.wireOp",EDGE,"E15.33.10.0"),sQuery(id+"F0.wireOp",EDGE,"E15.37.10.0"),sQuery(id+"F0.wireOp",EDGE,"E15.40.10.0"),sQuery(id+"F0.wireOp",EDGE,"E15.2.11.0"),sQuery(id+"F0.wireOp",EDGE,"E15.4.11.0"),sQuery(id+"F0.wireOp",EDGE,"E15.7.11.0"),sQuery(id+"F0.wireOp",EDGE,"E15.11.11.0"),sQuery(id+"F0.wireOp",EDGE,"E15.15.11.0"),sQuery(id+"F0.wireOp",EDGE,"E15.19.11.0"),sQuery(id+"F0.wireOp",EDGE,"E15.22.11.0"),sQuery(id+"F0.wireOp",EDGE,"E15.25.11.0"),sQuery(id+"F0.wireOp",EDGE,"E15.29.11.0"),sQuery(id+"F0.wireOp",EDGE,"E15.33.11.0"),sQuery(id+"F0.wireOp",EDGE,"E15.37.11.0"),sQuery(id+"F0.wireOp",EDGE,"E15.40.11.0"),sQuery(id+"F0.wireOp",EDGE,"E15.2.12.0"),sQuery(id+"F0.wireOp",EDGE,"E15.4.12.0"),sQuery(id+"F0.wireOp",EDGE,"E15.7.12.0"),sQuery(id+"F0.wireOp",EDGE,"E15.11.12.0"),sQuery(id+"F0.wireOp",EDGE,"E15.15.12.0"),sQuery(id+"F0.wireOp",EDGE,"E15.19.12.0"),sQuery(id+"F0.wireOp",EDGE,"E15.22.12.0"),sQuery(id+"F0.wireOp",EDGE,"E15.25.12.0"),sQuery(id+"F0.wireOp",EDGE,"E15.29.12.0"),sQuery(id+"F0.wireOp",EDGE,"E15.33.12.0"),sQuery(id+"F0.wireOp",EDGE,"E15.37.12.0"),sQuery(id+"F0.wireOp",EDGE,"E15.40.12.0"),sQuery(id+"F0.wireOp",EDGE,"E15.2.13.0"),sQuery(id+"F0.wireOp",EDGE,"E15.4.13.0"),sQuery(id+"F0.wireOp",EDGE,"E15.7.13.0"),sQuery(id+"F0.wireOp",EDGE,"E15.11.13.0"),sQuery(id+"F0.wireOp",EDGE,"E15.15.13.0"),sQuery(id+"F0.wireOp",EDGE,"E15.19.13.0"),sQuery(id+"F0.wireOp",EDGE,"E15.22.13.0"),sQuery(id+"F0.wireOp",EDGE,"E15.25.13.0"),sQuery(id+"F0.wireOp",EDGE,"E15.29.13.0"),sQuery(id+"F0.wireOp",EDGE,"E15.33.13.0"),sQuery(id+"F0.wireOp",EDGE,"E15.37.13.0"),sQuery(id+"F0.wireOp",EDGE,"E15.40.13.0"),sQuery(id+"F0.wireOp",EDGE,"E15.2.14.0"),sQuery(id+"F0.wireOp",EDGE,"E15.4.14.0"),sQuery(id+"F0.wireOp",EDGE,"E15.7.14.0"),sQuery(id+"F0.wireOp",EDGE,"E15.11.14.0"),sQuery(id+"F0.wireOp",EDGE,"E15.15.14.0"),sQuery(id+"F0.wireOp",EDGE,"E15.19.14.0"),sQuery(id+"F0.wireOp",EDGE,"E15.22.14.0"),sQuery(id+"F0.wireOp",EDGE,"E15.25.14.0"),sQuery(id+"F0.wireOp",EDGE,"E15.29.14.0"),sQuery(id+"F0.wireOp",EDGE,"E15.33.14.0"),sQuery(id+"F0.wireOp",EDGE,"E15.37.14.0"),sQuery(id+"F0.wireOp",EDGE,"E15.40.14.0"),sQuery(id+"F0.wireOp",EDGE,"E15.2.15.0"),sQuery(id+"F0.wireOp",EDGE,"E15.4.15.0"),sQuery(id+"F0.wireOp",EDGE,"E15.7.15.0"),sQuery(id+"F0.wireOp",EDGE,"E15.11.15.0"),sQuery(id+"F0.wireOp",EDGE,"E15.15.15.0"),sQuery(id+"F0.wireOp",EDGE,"E15.19.15.0"),sQuery(id+"F0.wireOp",EDGE,"E15.22.15.0"),sQuery(id+"F0.wireOp",EDGE,"E15.25.15.0"),sQuery(id+"F0.wireOp",EDGE,"E15.29.15.0"),sQuery(id+"F0.wireOp",EDGE,"E15.33.15.0"),sQuery(id+"F0.wireOp",EDGE,"E15.37.15.0"),sQuery(id+"F0.wireOp",EDGE,"E15.40.15.0"),sQuery(id+"F0.wireOp",EDGE,"E15.2.16.0"),sQuery(id+"F0.wireOp",EDGE,"E15.4.16.0"),sQuery(id+"F0.wireOp",EDGE,"E15.7.16.0"),sQuery(id+"F0.wireOp",EDGE,"E15.11.16.0"),sQuery(id+"F0.wireOp",EDGE,"E15.15.16.0"),sQuery(id+"F0.wireOp",EDGE,"E15.19.16.0"),sQuery(id+"F0.wireOp",EDGE,"E15.22.16.0"),sQuery(id+"F0.wireOp",EDGE,"E15.25.16.0"),sQuery(id+"F0.wireOp",EDGE,"E15.29.16.0"),sQuery(id+"F0.wireOp",EDGE,"E15.33.16.0"),sQuery(id+"F0.wireOp",EDGE,"E15.37.16.0"),sQuery(id+"F0.wireOp",EDGE,"E15.40.16.0"),sQuery(id+"F0.wireOp",EDGE,"E15.2.17.0"),sQuery(id+"F0.wireOp",EDGE,"E15.4.17.0"),sQuery(id+"F0.wireOp",EDGE,"E15.7.17.0"),sQuery(id+"F0.wireOp",EDGE,"E15.11.17.0"),sQuery(id+"F0.wireOp",EDGE,"E15.15.17.0"),sQuery(id+"F0.wireOp",EDGE,"E15.19.17.0"),sQuery(id+"F0.wireOp",EDGE,"E15.22.17.0"),sQuery(id+"F0.wireOp",EDGE,"E15.25.17.0"),sQuery(id+"F0.wireOp",EDGE,"E15.29.17.0"),sQuery(id+"F0.wireOp",EDGE,"E15.33.17.0"),sQuery(id+"F0.wireOp",EDGE,"E15.37.17.0"),sQuery(id+"F0.wireOp",EDGE,"E15.40.17.0"),sQuery(id+"F0.wireOp",EDGE,"E15.2.18.0"),sQuery(id+"F0.wireOp",EDGE,"E15.4.18.0"),sQuery(id+"F0.wireOp",EDGE,"E15.7.18.0"),sQuery(id+"F0.wireOp",EDGE,"E15.11.18.0"),sQuery(id+"F0.wireOp",EDGE,"E15.15.18.0"),sQuery(id+"F0.wireOp",EDGE,"E15.19.18.0"),sQuery(id+"F0.wireOp",EDGE,"E15.22.18.0"),sQuery(id+"F0.wireOp",EDGE,"E15.25.18.0"),sQuery(id+"F0.wireOp",EDGE,"E15.29.18.0"),sQuery(id+"F0.wireOp",EDGE,"E15.33.18.0"),sQuery(id+"F0.wireOp",EDGE,"E15.37.18.0"),sQuery(id+"F0.wireOp",EDGE,"E15.40.18.0"),sQuery(id+"F0.wireOp",EDGE,"E15.2.19.0"),sQuery(id+"F0.wireOp",EDGE,"E15.4.19.0"),sQuery(id+"F0.wireOp",EDGE,"E15.7.19.0"),sQuery(id+"F0.wireOp",EDGE,"E15.11.19.0"),sQuery(id+"F0.wireOp",EDGE,"E15.15.19.0"),sQuery(id+"F0.wireOp",EDGE,"E15.19.19.0"),sQuery(id+"F0.wireOp",EDGE,"E15.22.19.0"),sQuery(id+"F0.wireOp",EDGE,"E15.25.19.0"),sQuery(id+"F0.wireOp",EDGE,"E15.29.19.0"),sQuery(id+"F0.wireOp",EDGE,"E15.33.19.0"),sQuery(id+"F0.wireOp",EDGE,"E15.37.19.0"),sQuery(id+"F0.wireOp",EDGE,"E15.40.19.0"),sQuery(id+"F0.wireOp",EDGE,"E15.2.20.0"),sQuery(id+"F0.wireOp",EDGE,"E15.4.20.0"),sQuery(id+"F0.wireOp",EDGE,"E15.7.20.0"),sQuery(id+"F0.wireOp",EDGE,"E15.11.20.0"),sQuery(id+"F0.wireOp",EDGE,"E15.15.20.0"),sQuery(id+"F0.wireOp",EDGE,"E15.19.20.0"),sQuery(id+"F0.wireOp",EDGE,"E15.22.20.0"),sQuery(id+"F0.wireOp",EDGE,"E15.25.20.0"),sQuery(id+"F0.wireOp",EDGE,"E15.29.20.0"),sQuery(id+"F0.wireOp",EDGE,"E15.33.20.0"),sQuery(id+"F0.wireOp",EDGE,"E15.37.20.0"),sQuery(id+"F0.wireOp",EDGE,"E15.40.20.0"),sQuery(id+"F0.wireOp",EDGE,"E15.2.21.0"),sQuery(id+"F0.wireOp",EDGE,"E15.4.21.0"),sQuery(id+"F0.wireOp",EDGE,"E15.7.21.0"),sQuery(id+"F0.wireOp",EDGE,"E15.11.21.0"),sQuery(id+"F0.wireOp",EDGE,"E15.15.21.0"),sQuery(id+"F0.wireOp",EDGE,"E15.19.21.0"),sQuery(id+"F0.wireOp",EDGE,"E15.22.21.0"),sQuery(id+"F0.wireOp",EDGE,"E15.25.21.0"),sQuery(id+"F0.wireOp",EDGE,"E15.29.21.0"),sQuery(id+"F0.wireOp",EDGE,"E15.33.21.0"),sQuery(id+"F0.wireOp",EDGE,"E15.37.21.0"),sQuery(id+"F0.wireOp",EDGE,"E15.40.21.0"),sQuery(id+"F0.wireOp",EDGE,"E15.2.22.0"),sQuery(id+"F0.wireOp",EDGE,"E15.4.22.0"),sQuery(id+"F0.wireOp",EDGE,"E15.7.22.0"),sQuery(id+"F0.wireOp",EDGE,"E15.11.22.0"),sQuery(id+"F0.wireOp",EDGE,"E15.15.22.0"),sQuery(id+"F0.wireOp",EDGE,"E15.19.22.0"),sQuery(id+"F0.wireOp",EDGE,"E15.22.22.0"),sQuery(id+"F0.wireOp",EDGE,"E15.25.22.0"),sQuery(id+"F0.wireOp",EDGE,"E15.29.22.0"),sQuery(id+"F0.wireOp",EDGE,"E15.33.22.0"),sQuery(id+"F0.wireOp",EDGE,"E15.37.22.0"),sQuery(id+"F0.wireOp",EDGE,"E15.40.22.0"),sQuery(id+"F0.wireOp",EDGE,"E15.2.23.0"),sQuery(id+"F0.wireOp",EDGE,"E15.4.23.0"),sQuery(id+"F0.wireOp",EDGE,"E15.7.23.0"),sQuery(id+"F0.wireOp",EDGE,"E15.11.23.0"),sQuery(id+"F0.wireOp",EDGE,"E15.15.23.0"),sQuery(id+"F0.wireOp",EDGE,"E15.19.23.0"),sQuery(id+"F0.wireOp",EDGE,"E15.22.23.0"),sQuery(id+"F0.wireOp",EDGE,"E15.25.23.0"),sQuery(id+"F0.wireOp",EDGE,"E15.29.23.0"),sQuery(id+"F0.wireOp",EDGE,"E15.33.23.0"),sQuery(id+"F0.wireOp",EDGE,"E15.37.23.0"),sQuery(id+"F0.wireOp",EDGE,"E15.40.23.0"),sQuery(id+"F0.wireOp",EDGE,"E16.trimOffspring"),sQuery(id+"F0.wireOp",EDGE,"E17.trimOffspring"),sQuery(id+"F0.wireOp",EDGE,"E18.trimOffspring"),sQuery(id+"F0.wireOp",EDGE,"E19.trimOffspring"),sQuery(id+"F0.wireOp",EDGE,"E20.trimOffspring"),sQuery(id+"F0.wireOp",EDGE,"E21.trimOffspring"),sQuery(id+"F0.wireOp",EDGE,"E22.trimOffspring"),sQuery(id+"F0.wireOp",EDGE,"E23.trimOffspring"),sQuery(id+"F0.wireOp",EDGE,"E24.trimOffspring"),sQuery(id+"F0.wireOp",EDGE,"E25.trimOffspring"),sQuery(id+"F0.wireOp",EDGE,"E26.trimOffspring"),sQuery(id+"F0.wireOp",EDGE,"E27.trimOffspring"),sQuery(id+"F0.wireOp",EDGE,"E28.trimOffspring"),sQuery(id+"F0.wireOp",EDGE,"E29.trimOffspring"),sQuery(id+"F0.wireOp",EDGE,"E30.trimOffspring"),sQuery(id+"F0.wireOp",EDGE,"E31.trimOffspring"),sQuery(id+"F0.wireOp",EDGE,"E32.trimOffspring"),sQuery(id+"F0.wireOp",EDGE,"E33.trimOffspring"),sQuery(id+"F0.wireOp",EDGE,"E34.trimOffspring"),sQuery(id+"F0.wireOp",EDGE,"E35.trimOffspring"),sQuery(id+"F0.wireOp",EDGE,"E36.trimOffspring"),sQuery(id+"F0.wireOp",EDGE,"E37.trimOffspring"),sQuery(id+"F0.wireOp",EDGE,"E38.trimOffspring")])],"isStart":true});
            var sketch = newSketch(context, id + "F4", { "sketchPlane" : qUnion([Q0])});
            skCircle(sketch, "E40", {"center": v(0, 0) * mm, "radius": 3.18 * mm});
            skSolve(sketch);
        }
        {
            var Q0;
            Q0=qSketchRegion(id+"F4",true);
            extrude(context, id + "F5", {"entities" : qUnion([Q0]), "operationType" : NewBodyOperationType.REMOVE, "oppositeDirection" : true, "depth" : 5.08 * mm});
        }
        {
            var Q0;
            Q0=makeQuery(id+"F1.opExtrude","CAP_FACE",FACE,{"disambiguationData":[OSD([sQuery(id+"F0.wireOp",EDGE,"E0"),sQuery(id+"F0.wireOp",EDGE,"E1.trimOffspring"),sQuery(id+"F0.wireOp",EDGE,"E2"),sQuery(id+"F0.wireOp",EDGE,"E3"),sQuery(id+"F0.wireOp",EDGE,"E4.MirrorCS"),sQuery(id+"F0.wireOp",EDGE,"E5.MirrorCS"),sQuery(id+"F0.wireOp",EDGE,"E6.MirrorCS"),sQuery(id+"F0.wireOp",EDGE,"E8.filletArc"),sQuery(id+"F0.wireOp",EDGE,"E9.filletArc"),sQuery(id+"F0.wireOp",EDGE,"E10.filletArc"),sQuery(id+"F0.wireOp",EDGE,"E11.filletArc"),sQuery(id+"F0.wireOp",EDGE,"E12.filletArc"),sQuery(id+"F0.wireOp",EDGE,"E13.filletArc"),sQuery(id+"F0.wireOp",EDGE,"E14.1.0"),sQuery(id+"F0.wireOp",EDGE,"E14.1.1"),sQuery(id+"F0.wireOp",EDGE,"E14.1.2"),sQuery(id+"F0.wireOp",EDGE,"E14.1.3"),sQuery(id+"F0.wireOp",EDGE,"E14.1.4"),sQuery(id+"F0.wireOp",EDGE,"E14.1.5"),sQuery(id+"F0.wireOp",EDGE,"E14.1.6"),sQuery(id+"F0.wireOp",EDGE,"E14.1.7"),sQuery(id+"F0.wireOp",EDGE,"E14.1.8"),sQuery(id+"F0.wireOp",EDGE,"E14.1.9"),sQuery(id+"F0.wireOp",EDGE,"E14.1.10"),sQuery(id+"F0.wireOp",EDGE,"E14.1.11"),sQuery(id+"F0.wireOp",EDGE,"E14.2.0"),sQuery(id+"F0.wireOp",EDGE,"E14.2.1"),sQuery(id+"F0.wireOp",EDGE,"E14.2.2"),sQuery(id+"F0.wireOp",EDGE,"E14.2.3"),sQuery(id+"F0.wireOp",EDGE,"E14.2.4"),sQuery(id+"F0.wireOp",EDGE,"E14.2.5"),sQuery(id+"F0.wireOp",EDGE,"E14.2.6"),sQuery(id+"F0.wireOp",EDGE,"E14.2.7"),sQuery(id+"F0.wireOp",EDGE,"E14.2.8"),sQuery(id+"F0.wireOp",EDGE,"E14.2.9"),sQuery(id+"F0.wireOp",EDGE,"E14.2.10"),sQuery(id+"F0.wireOp",EDGE,"E14.2.11"),sQuery(id+"F0.wireOp",EDGE,"E15.2.3.0"),sQuery(id+"F0.wireOp",EDGE,"E15.4.3.0"),sQuery(id+"F0.wireOp",EDGE,"E15.7.3.0"),sQuery(id+"F0.wireOp",EDGE,"E15.11.3.0"),sQuery(id+"F0.wireOp",EDGE,"E15.15.3.0"),sQuery(id+"F0.wireOp",EDGE,"E15.19.3.0"),sQuery(id+"F0.wireOp",EDGE,"E15.22.3.0"),sQuery(id+"F0.wireOp",EDGE,"E15.25.3.0"),sQuery(id+"F0.wireOp",EDGE,"E15.29.3.0"),sQuery(id+"F0.wireOp",EDGE,"E15.33.3.0"),sQuery(id+"F0.wireOp",EDGE,"E15.37.3.0"),sQuery(id+"F0.wireOp",EDGE,"E15.40.3.0"),sQuery(id+"F0.wireOp",EDGE,"E15.2.4.0"),sQuery(id+"F0.wireOp",EDGE,"E15.4.4.0"),sQuery(id+"F0.wireOp",EDGE,"E15.7.4.0"),sQuery(id+"F0.wireOp",EDGE,"E15.11.4.0"),sQuery(id+"F0.wireOp",EDGE,"E15.15.4.0"),sQuery(id+"F0.wireOp",EDGE,"E15.19.4.0"),sQuery(id+"F0.wireOp",EDGE,"E15.22.4.0"),sQuery(id+"F0.wireOp",EDGE,"E15.25.4.0"),sQuery(id+"F0.wireOp",EDGE,"E15.29.4.0"),sQuery(id+"F0.wireOp",EDGE,"E15.33.4.0"),sQuery(id+"F0.wireOp",EDGE,"E15.37.4.0"),sQuery(id+"F0.wireOp",EDGE,"E15.40.4.0"),sQuery(id+"F0.wireOp",EDGE,"E15.2.5.0"),sQuery(id+"F0.wireOp",EDGE,"E15.4.5.0"),sQuery(id+"F0.wireOp",EDGE,"E15.7.5.0"),sQuery(id+"F0.wireOp",EDGE,"E15.11.5.0"),sQuery(id+"F0.wireOp",EDGE,"E15.15.5.0"),sQuery(id+"F0.wireOp",EDGE,"E15.19.5.0"),sQuery(id+"F0.wireOp",EDGE,"E15.22.5.0"),sQuery(id+"F0.wireOp",EDGE,"E15.25.5.0"),sQuery(id+"F0.wireOp",EDGE,"E15.29.5.0"),sQuery(id+"F0.wireOp",EDGE,"E15.33.5.0"),sQuery(id+"F0.wireOp",EDGE,"E15.37.5.0"),sQuery(id+"F0.wireOp",EDGE,"E15.40.5.0"),sQuery(id+"F0.wireOp",EDGE,"E15.2.6.0"),sQuery(id+"F0.wireOp",EDGE,"E15.4.6.0"),sQuery(id+"F0.wireOp",EDGE,"E15.7.6.0"),sQuery(id+"F0.wireOp",EDGE,"E15.11.6.0"),sQuery(id+"F0.wireOp",EDGE,"E15.15.6.0"),sQuery(id+"F0.wireOp",EDGE,"E15.19.6.0"),sQuery(id+"F0.wireOp",EDGE,"E15.22.6.0"),sQuery(id+"F0.wireOp",EDGE,"E15.25.6.0"),sQuery(id+"F0.wireOp",EDGE,"E15.29.6.0"),sQuery(id+"F0.wireOp",EDGE,"E15.33.6.0"),sQuery(id+"F0.wireOp",EDGE,"E15.37.6.0"),sQuery(id+"F0.wireOp",EDGE,"E15.40.6.0"),sQuery(id+"F0.wireOp",EDGE,"E15.2.7.0"),sQuery(id+"F0.wireOp",EDGE,"E15.4.7.0"),sQuery(id+"F0.wireOp",EDGE,"E15.7.7.0"),sQuery(id+"F0.wireOp",EDGE,"E15.11.7.0"),sQuery(id+"F0.wireOp",EDGE,"E15.15.7.0"),sQuery(id+"F0.wireOp",EDGE,"E15.19.7.0"),sQuery(id+"F0.wireOp",EDGE,"E15.22.7.0"),sQuery(id+"F0.wireOp",EDGE,"E15.25.7.0"),sQuery(id+"F0.wireOp",EDGE,"E15.29.7.0"),sQuery(id+"F0.wireOp",EDGE,"E15.33.7.0"),sQuery(id+"F0.wireOp",EDGE,"E15.37.7.0"),sQuery(id+"F0.wireOp",EDGE,"E15.40.7.0"),sQuery(id+"F0.wireOp",EDGE,"E15.2.8.0"),sQuery(id+"F0.wireOp",EDGE,"E15.4.8.0"),sQuery(id+"F0.wireOp",EDGE,"E15.7.8.0"),sQuery(id+"F0.wireOp",EDGE,"E15.11.8.0"),sQuery(id+"F0.wireOp",EDGE,"E15.15.8.0"),sQuery(id+"F0.wireOp",EDGE,"E15.19.8.0"),sQuery(id+"F0.wireOp",EDGE,"E15.22.8.0"),sQuery(id+"F0.wireOp",EDGE,"E15.25.8.0"),sQuery(id+"F0.wireOp",EDGE,"E15.29.8.0"),sQuery(id+"F0.wireOp",EDGE,"E15.33.8.0"),sQuery(id+"F0.wireOp",EDGE,"E15.37.8.0"),sQuery(id+"F0.wireOp",EDGE,"E15.40.8.0"),sQuery(id+"F0.wireOp",EDGE,"E15.2.9.0"),sQuery(id+"F0.wireOp",EDGE,"E15.4.9.0"),sQuery(id+"F0.wireOp",EDGE,"E15.7.9.0"),sQuery(id+"F0.wireOp",EDGE,"E15.11.9.0"),sQuery(id+"F0.wireOp",EDGE,"E15.15.9.0"),sQuery(id+"F0.wireOp",EDGE,"E15.19.9.0"),sQuery(id+"F0.wireOp",EDGE,"E15.22.9.0"),sQuery(id+"F0.wireOp",EDGE,"E15.25.9.0"),sQuery(id+"F0.wireOp",EDGE,"E15.29.9.0"),sQuery(id+"F0.wireOp",EDGE,"E15.33.9.0"),sQuery(id+"F0.wireOp",EDGE,"E15.37.9.0"),sQuery(id+"F0.wireOp",EDGE,"E15.40.9.0"),sQuery(id+"F0.wireOp",EDGE,"E15.2.10.0"),sQuery(id+"F0.wireOp",EDGE,"E15.4.10.0"),sQuery(id+"F0.wireOp",EDGE,"E15.7.10.0"),sQuery(id+"F0.wireOp",EDGE,"E15.11.10.0"),sQuery(id+"F0.wireOp",EDGE,"E15.15.10.0"),sQuery(id+"F0.wireOp",EDGE,"E15.19.10.0"),sQuery(id+"F0.wireOp",EDGE,"E15.22.10.0"),sQuery(id+"F0.wireOp",EDGE,"E15.25.10.0"),sQuery(id+"F0.wireOp",EDGE,"E15.29.10.0"),sQuery(id+"F0.wireOp",EDGE,"E15.33.10.0"),sQuery(id+"F0.wireOp",EDGE,"E15.37.10.0"),sQuery(id+"F0.wireOp",EDGE,"E15.40.10.0"),sQuery(id+"F0.wireOp",EDGE,"E15.2.11.0"),sQuery(id+"F0.wireOp",EDGE,"E15.4.11.0"),sQuery(id+"F0.wireOp",EDGE,"E15.7.11.0"),sQuery(id+"F0.wireOp",EDGE,"E15.11.11.0"),sQuery(id+"F0.wireOp",EDGE,"E15.15.11.0"),sQuery(id+"F0.wireOp",EDGE,"E15.19.11.0"),sQuery(id+"F0.wireOp",EDGE,"E15.22.11.0"),sQuery(id+"F0.wireOp",EDGE,"E15.25.11.0"),sQuery(id+"F0.wireOp",EDGE,"E15.29.11.0"),sQuery(id+"F0.wireOp",EDGE,"E15.33.11.0"),sQuery(id+"F0.wireOp",EDGE,"E15.37.11.0"),sQuery(id+"F0.wireOp",EDGE,"E15.40.11.0"),sQuery(id+"F0.wireOp",EDGE,"E15.2.12.0"),sQuery(id+"F0.wireOp",EDGE,"E15.4.12.0"),sQuery(id+"F0.wireOp",EDGE,"E15.7.12.0"),sQuery(id+"F0.wireOp",EDGE,"E15.11.12.0"),sQuery(id+"F0.wireOp",EDGE,"E15.15.12.0"),sQuery(id+"F0.wireOp",EDGE,"E15.19.12.0"),sQuery(id+"F0.wireOp",EDGE,"E15.22.12.0"),sQuery(id+"F0.wireOp",EDGE,"E15.25.12.0"),sQuery(id+"F0.wireOp",EDGE,"E15.29.12.0"),sQuery(id+"F0.wireOp",EDGE,"E15.33.12.0"),sQuery(id+"F0.wireOp",EDGE,"E15.37.12.0"),sQuery(id+"F0.wireOp",EDGE,"E15.40.12.0"),sQuery(id+"F0.wireOp",EDGE,"E15.2.13.0"),sQuery(id+"F0.wireOp",EDGE,"E15.4.13.0"),sQuery(id+"F0.wireOp",EDGE,"E15.7.13.0"),sQuery(id+"F0.wireOp",EDGE,"E15.11.13.0"),sQuery(id+"F0.wireOp",EDGE,"E15.15.13.0"),sQuery(id+"F0.wireOp",EDGE,"E15.19.13.0"),sQuery(id+"F0.wireOp",EDGE,"E15.22.13.0"),sQuery(id+"F0.wireOp",EDGE,"E15.25.13.0"),sQuery(id+"F0.wireOp",EDGE,"E15.29.13.0"),sQuery(id+"F0.wireOp",EDGE,"E15.33.13.0"),sQuery(id+"F0.wireOp",EDGE,"E15.37.13.0"),sQuery(id+"F0.wireOp",EDGE,"E15.40.13.0"),sQuery(id+"F0.wireOp",EDGE,"E15.2.14.0"),sQuery(id+"F0.wireOp",EDGE,"E15.4.14.0"),sQuery(id+"F0.wireOp",EDGE,"E15.7.14.0"),sQuery(id+"F0.wireOp",EDGE,"E15.11.14.0"),sQuery(id+"F0.wireOp",EDGE,"E15.15.14.0"),sQuery(id+"F0.wireOp",EDGE,"E15.19.14.0"),sQuery(id+"F0.wireOp",EDGE,"E15.22.14.0"),sQuery(id+"F0.wireOp",EDGE,"E15.25.14.0"),sQuery(id+"F0.wireOp",EDGE,"E15.29.14.0"),sQuery(id+"F0.wireOp",EDGE,"E15.33.14.0"),sQuery(id+"F0.wireOp",EDGE,"E15.37.14.0"),sQuery(id+"F0.wireOp",EDGE,"E15.40.14.0"),sQuery(id+"F0.wireOp",EDGE,"E15.2.15.0"),sQuery(id+"F0.wireOp",EDGE,"E15.4.15.0"),sQuery(id+"F0.wireOp",EDGE,"E15.7.15.0"),sQuery(id+"F0.wireOp",EDGE,"E15.11.15.0"),sQuery(id+"F0.wireOp",EDGE,"E15.15.15.0"),sQuery(id+"F0.wireOp",EDGE,"E15.19.15.0"),sQuery(id+"F0.wireOp",EDGE,"E15.22.15.0"),sQuery(id+"F0.wireOp",EDGE,"E15.25.15.0"),sQuery(id+"F0.wireOp",EDGE,"E15.29.15.0"),sQuery(id+"F0.wireOp",EDGE,"E15.33.15.0"),sQuery(id+"F0.wireOp",EDGE,"E15.37.15.0"),sQuery(id+"F0.wireOp",EDGE,"E15.40.15.0"),sQuery(id+"F0.wireOp",EDGE,"E15.2.16.0"),sQuery(id+"F0.wireOp",EDGE,"E15.4.16.0"),sQuery(id+"F0.wireOp",EDGE,"E15.7.16.0"),sQuery(id+"F0.wireOp",EDGE,"E15.11.16.0"),sQuery(id+"F0.wireOp",EDGE,"E15.15.16.0"),sQuery(id+"F0.wireOp",EDGE,"E15.19.16.0"),sQuery(id+"F0.wireOp",EDGE,"E15.22.16.0"),sQuery(id+"F0.wireOp",EDGE,"E15.25.16.0"),sQuery(id+"F0.wireOp",EDGE,"E15.29.16.0"),sQuery(id+"F0.wireOp",EDGE,"E15.33.16.0"),sQuery(id+"F0.wireOp",EDGE,"E15.37.16.0"),sQuery(id+"F0.wireOp",EDGE,"E15.40.16.0"),sQuery(id+"F0.wireOp",EDGE,"E15.2.17.0"),sQuery(id+"F0.wireOp",EDGE,"E15.4.17.0"),sQuery(id+"F0.wireOp",EDGE,"E15.7.17.0"),sQuery(id+"F0.wireOp",EDGE,"E15.11.17.0"),sQuery(id+"F0.wireOp",EDGE,"E15.15.17.0"),sQuery(id+"F0.wireOp",EDGE,"E15.19.17.0"),sQuery(id+"F0.wireOp",EDGE,"E15.22.17.0"),sQuery(id+"F0.wireOp",EDGE,"E15.25.17.0"),sQuery(id+"F0.wireOp",EDGE,"E15.29.17.0"),sQuery(id+"F0.wireOp",EDGE,"E15.33.17.0"),sQuery(id+"F0.wireOp",EDGE,"E15.37.17.0"),sQuery(id+"F0.wireOp",EDGE,"E15.40.17.0"),sQuery(id+"F0.wireOp",EDGE,"E15.2.18.0"),sQuery(id+"F0.wireOp",EDGE,"E15.4.18.0"),sQuery(id+"F0.wireOp",EDGE,"E15.7.18.0"),sQuery(id+"F0.wireOp",EDGE,"E15.11.18.0"),sQuery(id+"F0.wireOp",EDGE,"E15.15.18.0"),sQuery(id+"F0.wireOp",EDGE,"E15.19.18.0"),sQuery(id+"F0.wireOp",EDGE,"E15.22.18.0"),sQuery(id+"F0.wireOp",EDGE,"E15.25.18.0"),sQuery(id+"F0.wireOp",EDGE,"E15.29.18.0"),sQuery(id+"F0.wireOp",EDGE,"E15.33.18.0"),sQuery(id+"F0.wireOp",EDGE,"E15.37.18.0"),sQuery(id+"F0.wireOp",EDGE,"E15.40.18.0"),sQuery(id+"F0.wireOp",EDGE,"E15.2.19.0"),sQuery(id+"F0.wireOp",EDGE,"E15.4.19.0"),sQuery(id+"F0.wireOp",EDGE,"E15.7.19.0"),sQuery(id+"F0.wireOp",EDGE,"E15.11.19.0"),sQuery(id+"F0.wireOp",EDGE,"E15.15.19.0"),sQuery(id+"F0.wireOp",EDGE,"E15.19.19.0"),sQuery(id+"F0.wireOp",EDGE,"E15.22.19.0"),sQuery(id+"F0.wireOp",EDGE,"E15.25.19.0"),sQuery(id+"F0.wireOp",EDGE,"E15.29.19.0"),sQuery(id+"F0.wireOp",EDGE,"E15.33.19.0"),sQuery(id+"F0.wireOp",EDGE,"E15.37.19.0"),sQuery(id+"F0.wireOp",EDGE,"E15.40.19.0"),sQuery(id+"F0.wireOp",EDGE,"E15.2.20.0"),sQuery(id+"F0.wireOp",EDGE,"E15.4.20.0"),sQuery(id+"F0.wireOp",EDGE,"E15.7.20.0"),sQuery(id+"F0.wireOp",EDGE,"E15.11.20.0"),sQuery(id+"F0.wireOp",EDGE,"E15.15.20.0"),sQuery(id+"F0.wireOp",EDGE,"E15.19.20.0"),sQuery(id+"F0.wireOp",EDGE,"E15.22.20.0"),sQuery(id+"F0.wireOp",EDGE,"E15.25.20.0"),sQuery(id+"F0.wireOp",EDGE,"E15.29.20.0"),sQuery(id+"F0.wireOp",EDGE,"E15.33.20.0"),sQuery(id+"F0.wireOp",EDGE,"E15.37.20.0"),sQuery(id+"F0.wireOp",EDGE,"E15.40.20.0"),sQuery(id+"F0.wireOp",EDGE,"E15.2.21.0"),sQuery(id+"F0.wireOp",EDGE,"E15.4.21.0"),sQuery(id+"F0.wireOp",EDGE,"E15.7.21.0"),sQuery(id+"F0.wireOp",EDGE,"E15.11.21.0"),sQuery(id+"F0.wireOp",EDGE,"E15.15.21.0"),sQuery(id+"F0.wireOp",EDGE,"E15.19.21.0"),sQuery(id+"F0.wireOp",EDGE,"E15.22.21.0"),sQuery(id+"F0.wireOp",EDGE,"E15.25.21.0"),sQuery(id+"F0.wireOp",EDGE,"E15.29.21.0"),sQuery(id+"F0.wireOp",EDGE,"E15.33.21.0"),sQuery(id+"F0.wireOp",EDGE,"E15.37.21.0"),sQuery(id+"F0.wireOp",EDGE,"E15.40.21.0"),sQuery(id+"F0.wireOp",EDGE,"E15.2.22.0"),sQuery(id+"F0.wireOp",EDGE,"E15.4.22.0"),sQuery(id+"F0.wireOp",EDGE,"E15.7.22.0"),sQuery(id+"F0.wireOp",EDGE,"E15.11.22.0"),sQuery(id+"F0.wireOp",EDGE,"E15.15.22.0"),sQuery(id+"F0.wireOp",EDGE,"E15.19.22.0"),sQuery(id+"F0.wireOp",EDGE,"E15.22.22.0"),sQuery(id+"F0.wireOp",EDGE,"E15.25.22.0"),sQuery(id+"F0.wireOp",EDGE,"E15.29.22.0"),sQuery(id+"F0.wireOp",EDGE,"E15.33.22.0"),sQuery(id+"F0.wireOp",EDGE,"E15.37.22.0"),sQuery(id+"F0.wireOp",EDGE,"E15.40.22.0"),sQuery(id+"F0.wireOp",EDGE,"E15.2.23.0"),sQuery(id+"F0.wireOp",EDGE,"E15.4.23.0"),sQuery(id+"F0.wireOp",EDGE,"E15.7.23.0"),sQuery(id+"F0.wireOp",EDGE,"E15.11.23.0"),sQuery(id+"F0.wireOp",EDGE,"E15.15.23.0"),sQuery(id+"F0.wireOp",EDGE,"E15.19.23.0"),sQuery(id+"F0.wireOp",EDGE,"E15.22.23.0"),sQuery(id+"F0.wireOp",EDGE,"E15.25.23.0"),sQuery(id+"F0.wireOp",EDGE,"E15.29.23.0"),sQuery(id+"F0.wireOp",EDGE,"E15.33.23.0"),sQuery(id+"F0.wireOp",EDGE,"E15.37.23.0"),sQuery(id+"F0.wireOp",EDGE,"E15.40.23.0"),sQuery(id+"F0.wireOp",EDGE,"E16.trimOffspring"),sQuery(id+"F0.wireOp",EDGE,"E17.trimOffspring"),sQuery(id+"F0.wireOp",EDGE,"E18.trimOffspring"),sQuery(id+"F0.wireOp",EDGE,"E19.trimOffspring"),sQuery(id+"F0.wireOp",EDGE,"E20.trimOffspring"),sQuery(id+"F0.wireOp",EDGE,"E21.trimOffspring"),sQuery(id+"F0.wireOp",EDGE,"E22.trimOffspring"),sQuery(id+"F0.wireOp",EDGE,"E23.trimOffspring"),sQuery(id+"F0.wireOp",EDGE,"E24.trimOffspring"),sQuery(id+"F0.wireOp",EDGE,"E25.trimOffspring"),sQuery(id+"F0.wireOp",EDGE,"E26.trimOffspring"),sQuery(id+"F0.wireOp",EDGE,"E27.trimOffspring"),sQuery(id+"F0.wireOp",EDGE,"E28.trimOffspring"),sQuery(id+"F0.wireOp",EDGE,"E29.trimOffspring"),sQuery(id+"F0.wireOp",EDGE,"E30.trimOffspring"),sQuery(id+"F0.wireOp",EDGE,"E31.trimOffspring"),sQuery(id+"F0.wireOp",EDGE,"E32.trimOffspring"),sQuery(id+"F0.wireOp",EDGE,"E33.trimOffspring"),sQuery(id+"F0.wireOp",EDGE,"E34.trimOffspring"),sQuery(id+"F0.wireOp",EDGE,"E35.trimOffspring"),sQuery(id+"F0.wireOp",EDGE,"E36.trimOffspring"),sQuery(id+"F0.wireOp",EDGE,"E37.trimOffspring"),sQuery(id+"F0.wireOp",EDGE,"E38.trimOffspring")])],"isStart":true});
            var sketch = newSketch(context, id + "F6", { "sketchPlane" : qUnion([Q0])});
            skCircle(sketch, "E41.0", {"center": v(0, 0) * mm, "radius": 3.18 * mm});
            skSolve(sketch);
        }
        {
            var Q0;
            Q0=makeQuery(id+"F6.imprint","IMPRINT",FACE,{"disambiguationData":[TD([[makeQuery(id+"F6.imprint","IMPRINT",EDGE,{"derivedFrom":sQuery(id+"F6.wireOp",EDGE,"E41.0")}),1.0]])]});
            extrude(context, id + "F7", {"entities" : qUnion([Q0]), "operationType" : NewBodyOperationType.ADD, "depth" : 4 * mm, "symmetric" : true});
        }
    });
